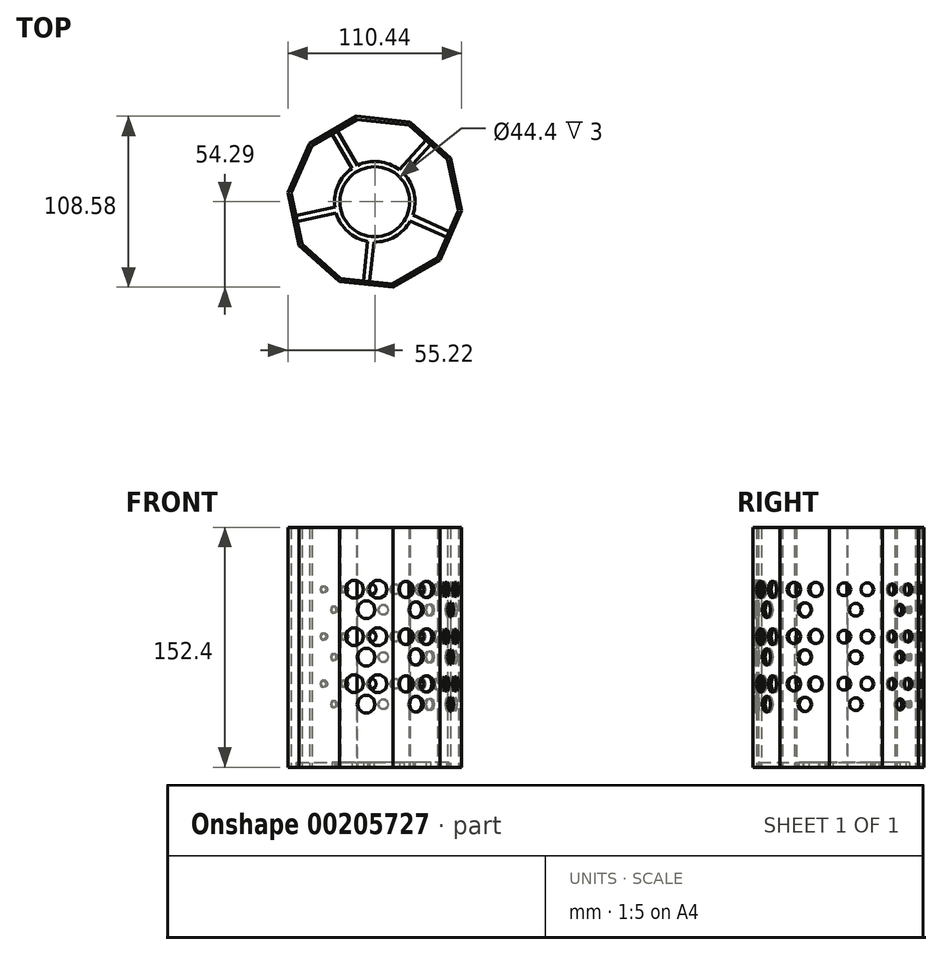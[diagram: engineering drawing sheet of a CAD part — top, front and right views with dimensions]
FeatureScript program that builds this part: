
annotation { "Feature Type Name" : "Feature", "Feature Type Description" : "" }
export const myFeature = defineFeature(function(context is Context, id is Id, definition is map)
    precondition{}
    {
        {
            var Q0;
            Q0=qCreatedBy(makeId("Top.planeOp"),FACE);
            var sketch = newSketch(context, id + "F0", { "sketchPlane" : qUnion([Q0])});
            skCircle(sketch, "E0.cCircle", {"center": v(0, 0) * mm, "radius": 50.8 * mm, "construction": true});
            skLineSegment(sketch, "E0.0", {"start": v(-39.74, 35.7) * mm, "end": v(-11.17, 52.23) * mm});
            skLineSegment(sketch, "E0.1", {"start": v(-11.17, 52.23) * mm, "end": v(21.67, 48.82) * mm});
            skLineSegment(sketch, "E0.2", {"start": v(21.67, 48.82) * mm, "end": v(46.23, 26.76) * mm});
            skLineSegment(sketch, "E0.3", {"start": v(46.23, 26.76) * mm, "end": v(53.13, -5.52) * mm});
            skLineSegment(sketch, "E0.4", {"start": v(53.13, -5.52) * mm, "end": v(39.74, -35.7) * mm});
            skLineSegment(sketch, "E0.5", {"start": v(39.74, -35.7) * mm, "end": v(11.17, -52.23) * mm});
            skLineSegment(sketch, "E0.6", {"start": v(11.17, -52.23) * mm, "end": v(-21.67, -48.82) * mm});
            skLineSegment(sketch, "E0.7", {"start": v(-21.67, -48.82) * mm, "end": v(-46.23, -26.76) * mm});
            skLineSegment(sketch, "E0.8", {"start": v(-46.23, -26.76) * mm, "end": v(-53.13, 5.52) * mm});
            skLineSegment(sketch, "E0.9", {"start": v(-53.13, 5.52) * mm, "end": v(-39.74, 35.7) * mm});
            skPoint(sketch, "E0.0.midPoint", {"position": v(-25.45, 43.96) * mm});
            skLineSegment(sketch, "E1.0", {"start": v(-41.3, 37.1) * mm, "end": v(-11.6, 54.3) * mm});
            skLineSegment(sketch, "E1.1", {"start": v(-55.22, 5.74) * mm, "end": v(-41.3, 37.1) * mm});
            skLineSegment(sketch, "E1.2", {"start": v(-11.6, 54.3) * mm, "end": v(22.52, 50.74) * mm});
            skLineSegment(sketch, "E1.3", {"start": v(-48.05, -27.82) * mm, "end": v(-55.22, 5.74) * mm});
            skLineSegment(sketch, "E1.4", {"start": v(-22.52, -50.74) * mm, "end": v(-48.05, -27.82) * mm});
            skLineSegment(sketch, "E1.5", {"start": v(11.6, -54.3) * mm, "end": v(-22.52, -50.74) * mm});
            skLineSegment(sketch, "E1.6", {"start": v(22.52, 50.74) * mm, "end": v(48.05, 27.82) * mm});
            skLineSegment(sketch, "E1.7", {"start": v(48.05, 27.82) * mm, "end": v(55.22, -5.74) * mm});
            skLineSegment(sketch, "E1.8", {"start": v(55.22, -5.74) * mm, "end": v(41.3, -37.1) * mm});
            skLineSegment(sketch, "E1.9", {"start": v(41.3, -37.1) * mm, "end": v(11.6, -54.3) * mm});
            skSolve(sketch);
        }
        {
            var Q0;
            Q0=makeQuery(id+"F0.imprint","IMPRINT",FACE,{"disambiguationData":[TD([[makeQuery(id+"F0.imprint","IMPRINT",EDGE,{"derivedFrom":sQuery(id+"F0.wireOp",EDGE,"E0.0")}),1.0]])]});
            extrude(context, id + "F1", {"entities" : qUnion([Q0]), "depth" : 152.4 * mm});
        }
        {
            var Q0;
            Q0=makeQuery(id+"F1.opExtrude","SWEPT_FACE",FACE,{"disambiguationData":[OSD([sQuery(id+"F0.wireOp",EDGE,"E1.5")])]});
            var sketch = newSketch(context, id + "F2", { "sketchPlane" : qUnion([Q0])});
            skCircle(sketch, "E2.cCircle", {"center": v(0, 40) * mm, "radius": 5.5 * mm, "construction": true});
            skLineSegment(sketch, "E2.0", {"start": v(-1.79, 45.5) * mm, "end": v(1.79, 45.5) * mm});
            skLineSegment(sketch, "E2.1", {"start": v(1.79, 45.5) * mm, "end": v(4.68, 43.4) * mm});
            skLineSegment(sketch, "E2.2", {"start": v(4.68, 43.4) * mm, "end": v(5.78, 40) * mm});
            skLineSegment(sketch, "E2.3", {"start": v(5.78, 40) * mm, "end": v(4.68, 36.6) * mm});
            skLineSegment(sketch, "E2.4", {"start": v(4.68, 36.6) * mm, "end": v(1.79, 34.5) * mm});
            skLineSegment(sketch, "E2.5", {"start": v(1.79, 34.5) * mm, "end": v(-1.79, 34.5) * mm});
            skLineSegment(sketch, "E2.6", {"start": v(-1.79, 34.5) * mm, "end": v(-4.68, 36.6) * mm});
            skLineSegment(sketch, "E2.7", {"start": v(-4.68, 36.6) * mm, "end": v(-5.78, 40) * mm});
            skLineSegment(sketch, "E2.8", {"start": v(-5.78, 40) * mm, "end": v(-4.68, 43.4) * mm});
            skLineSegment(sketch, "E2.9", {"start": v(-4.68, 43.4) * mm, "end": v(-1.79, 45.5) * mm});
            skPoint(sketch, "E2.0.midPoint", {"position": v(0, 45.5) * mm});
            skCircle(sketch, "E3.cCircle", {"center": v(-7.5, 53) * mm, "radius": 5.5 * mm, "construction": true});
            skLineSegment(sketch, "E3.0", {"start": v(-9.29, 58.5) * mm, "end": v(-5.71, 58.5) * mm});
            skLineSegment(sketch, "E3.1", {"start": v(-5.71, 58.5) * mm, "end": v(-2.82, 56.39) * mm});
            skLineSegment(sketch, "E3.2", {"start": v(-2.82, 56.39) * mm, "end": v(-1.72, 53) * mm});
            skLineSegment(sketch, "E3.3", {"start": v(-1.72, 53) * mm, "end": v(-2.82, 49.6) * mm});
            skLineSegment(sketch, "E3.4", {"start": v(-2.82, 49.6) * mm, "end": v(-5.71, 47.5) * mm});
            skLineSegment(sketch, "E3.5", {"start": v(-5.71, 47.5) * mm, "end": v(-9.29, 47.5) * mm});
            skLineSegment(sketch, "E3.6", {"start": v(-9.29, 47.5) * mm, "end": v(-12.18, 49.6) * mm});
            skLineSegment(sketch, "E3.7", {"start": v(-12.18, 49.6) * mm, "end": v(-13.28, 53) * mm});
            skLineSegment(sketch, "E3.8", {"start": v(-13.28, 53) * mm, "end": v(-12.18, 56.39) * mm});
            skLineSegment(sketch, "E3.9", {"start": v(-12.18, 56.39) * mm, "end": v(-9.29, 58.5) * mm});
            skPoint(sketch, "E3.0.midPoint", {"position": v(-7.5, 58.5) * mm});
            skCircle(sketch, "E4.cCircle", {"center": v(7.5, 53) * mm, "radius": 5.5 * mm, "construction": true});
            skLineSegment(sketch, "E4.0", {"start": v(5.71, 58.5) * mm, "end": v(9.29, 58.5) * mm});
            skLineSegment(sketch, "E4.1", {"start": v(9.29, 58.5) * mm, "end": v(12.18, 56.39) * mm});
            skLineSegment(sketch, "E4.2", {"start": v(12.18, 56.39) * mm, "end": v(13.28, 53) * mm});
            skLineSegment(sketch, "E4.3", {"start": v(13.28, 53) * mm, "end": v(12.18, 49.6) * mm});
            skLineSegment(sketch, "E4.4", {"start": v(12.18, 49.6) * mm, "end": v(9.29, 47.5) * mm});
            skLineSegment(sketch, "E4.5", {"start": v(9.29, 47.5) * mm, "end": v(5.71, 47.5) * mm});
            skLineSegment(sketch, "E4.6", {"start": v(5.71, 47.5) * mm, "end": v(2.82, 49.6) * mm});
            skLineSegment(sketch, "E4.7", {"start": v(2.82, 49.6) * mm, "end": v(1.72, 53) * mm});
            skLineSegment(sketch, "E4.8", {"start": v(1.72, 53) * mm, "end": v(2.82, 56.39) * mm});
            skLineSegment(sketch, "E4.9", {"start": v(2.82, 56.39) * mm, "end": v(5.71, 58.5) * mm});
            skPoint(sketch, "E4.0.midPoint", {"position": v(7.5, 58.5) * mm});
            skLineSegment(sketch, "E5", {"start": v(7.5, 53) * mm, "end": v(-7.5, 53) * mm, "construction": true});
            skLineSegment(sketch, "E6", {"start": v(0, 40) * mm, "end": v(-7.5, 53) * mm, "construction": true});
            skLineSegment(sketch, "E7", {"start": v(0, 40) * mm, "end": v(7.5, 53) * mm, "construction": true});
            skLineSegment(sketch, "E8", {"start": v(0, 0) * mm, "end": v(0, 152.4) * mm, "construction": true});
            skPoint(sketch, "E9.0.1.0", {"position": v(0, 75.5) * mm});
            skLineSegment(sketch, "E9.0.1.1", {"start": v(0, 70) * mm, "end": v(7.5, 83) * mm, "construction": true});
            skLineSegment(sketch, "E9.0.1.2", {"start": v(0, 70) * mm, "end": v(-7.5, 83) * mm, "construction": true});
            skLineSegment(sketch, "E9.0.1.3", {"start": v(7.5, 83) * mm, "end": v(-7.5, 83) * mm, "construction": true});
            skPoint(sketch, "E9.0.1.4", {"position": v(7.5, 88.5) * mm});
            skPoint(sketch, "E9.0.1.5", {"position": v(-7.5, 88.5) * mm});
            skLineSegment(sketch, "E9.0.1.6", {"start": v(-2.82, 86.39) * mm, "end": v(-1.72, 83) * mm});
            skLineSegment(sketch, "E9.0.1.7", {"start": v(13.28, 83) * mm, "end": v(12.18, 79.6) * mm});
            skLineSegment(sketch, "E9.0.1.8", {"start": v(2.82, 86.39) * mm, "end": v(5.71, 88.5) * mm});
            skCircle(sketch, "E9.0.1.9", {"center": v(7.5, 83) * mm, "radius": 5.5 * mm, "construction": true});
            skLineSegment(sketch, "E9.0.1.10", {"start": v(2.82, 79.6) * mm, "end": v(1.72, 83) * mm});
            skLineSegment(sketch, "E9.0.1.11", {"start": v(-5.78, 70) * mm, "end": v(-4.68, 73.4) * mm});
            skLineSegment(sketch, "E9.0.1.12", {"start": v(4.68, 73.4) * mm, "end": v(5.78, 70) * mm});
            skLineSegment(sketch, "E9.0.1.13", {"start": v(-9.29, 77.5) * mm, "end": v(-12.18, 79.6) * mm});
            skLineSegment(sketch, "E9.0.1.14", {"start": v(1.79, 75.5) * mm, "end": v(4.68, 73.4) * mm});
            skLineSegment(sketch, "E9.0.1.15", {"start": v(-2.82, 79.6) * mm, "end": v(-5.71, 77.5) * mm});
            skLineSegment(sketch, "E9.0.1.16", {"start": v(-9.29, 88.5) * mm, "end": v(-5.71, 88.5) * mm});
            skLineSegment(sketch, "E9.0.1.17", {"start": v(-5.71, 88.5) * mm, "end": v(-2.82, 86.39) * mm});
            skCircle(sketch, "E9.0.1.18", {"center": v(-7.5, 83) * mm, "radius": 5.5 * mm, "construction": true});
            skLineSegment(sketch, "E9.0.1.19", {"start": v(12.18, 79.6) * mm, "end": v(9.29, 77.5) * mm});
            skLineSegment(sketch, "E9.0.1.20", {"start": v(-12.18, 86.39) * mm, "end": v(-9.29, 88.5) * mm});
            skLineSegment(sketch, "E9.0.1.21", {"start": v(12.18, 86.39) * mm, "end": v(13.28, 83) * mm});
            skLineSegment(sketch, "E9.0.1.22", {"start": v(-4.68, 66.6) * mm, "end": v(-5.78, 70) * mm});
            skLineSegment(sketch, "E9.0.1.23", {"start": v(-13.28, 83) * mm, "end": v(-12.18, 86.39) * mm});
            skLineSegment(sketch, "E9.0.1.24", {"start": v(9.29, 77.5) * mm, "end": v(5.71, 77.5) * mm});
            skLineSegment(sketch, "E9.0.1.25", {"start": v(-4.68, 73.4) * mm, "end": v(-1.79, 75.5) * mm});
            skLineSegment(sketch, "E9.0.1.26", {"start": v(-12.18, 79.6) * mm, "end": v(-13.28, 83) * mm});
            skLineSegment(sketch, "E9.0.1.27", {"start": v(-1.79, 64.5) * mm, "end": v(-4.68, 66.6) * mm});
            skLineSegment(sketch, "E9.0.1.28", {"start": v(5.71, 77.5) * mm, "end": v(2.82, 79.6) * mm});
            skCircle(sketch, "E9.0.1.29", {"center": v(0, 70) * mm, "radius": 5.5 * mm, "construction": true});
            skLineSegment(sketch, "E9.0.1.30", {"start": v(-1.72, 83) * mm, "end": v(-2.82, 79.6) * mm});
            skLineSegment(sketch, "E9.0.1.31", {"start": v(1.72, 83) * mm, "end": v(2.82, 86.39) * mm});
            skLineSegment(sketch, "E9.0.1.32", {"start": v(9.29, 88.5) * mm, "end": v(12.18, 86.39) * mm});
            skLineSegment(sketch, "E9.0.1.33", {"start": v(5.78, 70) * mm, "end": v(4.68, 66.6) * mm});
            skLineSegment(sketch, "E9.0.1.34", {"start": v(4.68, 66.6) * mm, "end": v(1.79, 64.5) * mm});
            skLineSegment(sketch, "E9.0.1.35", {"start": v(5.71, 88.5) * mm, "end": v(9.29, 88.5) * mm});
            skLineSegment(sketch, "E9.0.1.36", {"start": v(-5.71, 77.5) * mm, "end": v(-9.29, 77.5) * mm});
            skLineSegment(sketch, "E9.0.1.37", {"start": v(1.79, 64.5) * mm, "end": v(-1.79, 64.5) * mm});
            skLineSegment(sketch, "E9.0.1.38", {"start": v(-1.79, 75.5) * mm, "end": v(1.79, 75.5) * mm});
            skPoint(sketch, "E9.0.2.0", {"position": v(0, 105.5) * mm});
            skLineSegment(sketch, "E9.0.2.1", {"start": v(0, 100) * mm, "end": v(7.5, 113) * mm, "construction": true});
            skLineSegment(sketch, "E9.0.2.2", {"start": v(0, 100) * mm, "end": v(-7.5, 113) * mm, "construction": true});
            skLineSegment(sketch, "E9.0.2.3", {"start": v(7.5, 113) * mm, "end": v(-7.5, 113) * mm, "construction": true});
            skPoint(sketch, "E9.0.2.4", {"position": v(7.5, 118.5) * mm});
            skPoint(sketch, "E9.0.2.5", {"position": v(-7.5, 118.5) * mm});
            skLineSegment(sketch, "E9.0.2.6", {"start": v(-2.82, 116.39) * mm, "end": v(-1.72, 113) * mm});
            skLineSegment(sketch, "E9.0.2.7", {"start": v(13.28, 113) * mm, "end": v(12.18, 109.6) * mm});
            skLineSegment(sketch, "E9.0.2.8", {"start": v(2.82, 116.39) * mm, "end": v(5.71, 118.5) * mm});
            skCircle(sketch, "E9.0.2.9", {"center": v(7.5, 113) * mm, "radius": 5.5 * mm, "construction": true});
            skLineSegment(sketch, "E9.0.2.10", {"start": v(2.82, 109.6) * mm, "end": v(1.72, 113) * mm});
            skLineSegment(sketch, "E9.0.2.11", {"start": v(-5.78, 100) * mm, "end": v(-4.68, 103.4) * mm});
            skLineSegment(sketch, "E9.0.2.12", {"start": v(4.68, 103.4) * mm, "end": v(5.78, 100) * mm});
            skLineSegment(sketch, "E9.0.2.13", {"start": v(-9.29, 107.5) * mm, "end": v(-12.18, 109.6) * mm});
            skLineSegment(sketch, "E9.0.2.14", {"start": v(1.79, 105.5) * mm, "end": v(4.68, 103.4) * mm});
            skLineSegment(sketch, "E9.0.2.15", {"start": v(-2.82, 109.6) * mm, "end": v(-5.71, 107.5) * mm});
            skLineSegment(sketch, "E9.0.2.16", {"start": v(-9.29, 118.5) * mm, "end": v(-5.71, 118.5) * mm});
            skLineSegment(sketch, "E9.0.2.17", {"start": v(-5.71, 118.5) * mm, "end": v(-2.82, 116.39) * mm});
            skCircle(sketch, "E9.0.2.18", {"center": v(-7.5, 113) * mm, "radius": 5.5 * mm, "construction": true});
            skLineSegment(sketch, "E9.0.2.19", {"start": v(12.18, 109.6) * mm, "end": v(9.29, 107.5) * mm});
            skLineSegment(sketch, "E9.0.2.20", {"start": v(-12.18, 116.39) * mm, "end": v(-9.29, 118.5) * mm});
            skLineSegment(sketch, "E9.0.2.21", {"start": v(12.18, 116.39) * mm, "end": v(13.28, 113) * mm});
            skLineSegment(sketch, "E9.0.2.22", {"start": v(-4.68, 96.6) * mm, "end": v(-5.78, 100) * mm});
            skLineSegment(sketch, "E9.0.2.23", {"start": v(-13.28, 113) * mm, "end": v(-12.18, 116.39) * mm});
            skLineSegment(sketch, "E9.0.2.24", {"start": v(9.29, 107.5) * mm, "end": v(5.71, 107.5) * mm});
            skLineSegment(sketch, "E9.0.2.25", {"start": v(-4.68, 103.4) * mm, "end": v(-1.79, 105.5) * mm});
            skLineSegment(sketch, "E9.0.2.26", {"start": v(-12.18, 109.6) * mm, "end": v(-13.28, 113) * mm});
            skLineSegment(sketch, "E9.0.2.27", {"start": v(-1.79, 94.5) * mm, "end": v(-4.68, 96.6) * mm});
            skLineSegment(sketch, "E9.0.2.28", {"start": v(5.71, 107.5) * mm, "end": v(2.82, 109.6) * mm});
            skCircle(sketch, "E9.0.2.29", {"center": v(0, 100) * mm, "radius": 5.5 * mm, "construction": true});
            skLineSegment(sketch, "E9.0.2.30", {"start": v(-1.72, 113) * mm, "end": v(-2.82, 109.6) * mm});
            skLineSegment(sketch, "E9.0.2.31", {"start": v(1.72, 113) * mm, "end": v(2.82, 116.39) * mm});
            skLineSegment(sketch, "E9.0.2.32", {"start": v(9.29, 118.5) * mm, "end": v(12.18, 116.39) * mm});
            skLineSegment(sketch, "E9.0.2.33", {"start": v(5.78, 100) * mm, "end": v(4.68, 96.6) * mm});
            skLineSegment(sketch, "E9.0.2.34", {"start": v(4.68, 96.6) * mm, "end": v(1.79, 94.5) * mm});
            skLineSegment(sketch, "E9.0.2.35", {"start": v(5.71, 118.5) * mm, "end": v(9.29, 118.5) * mm});
            skLineSegment(sketch, "E9.0.2.36", {"start": v(-5.71, 107.5) * mm, "end": v(-9.29, 107.5) * mm});
            skLineSegment(sketch, "E9.0.2.37", {"start": v(1.79, 94.5) * mm, "end": v(-1.79, 94.5) * mm});
            skLineSegment(sketch, "E9.0.2.38", {"start": v(-1.79, 105.5) * mm, "end": v(1.79, 105.5) * mm});
            skLineSegment(sketch, "E9.direction1", {"start": v(-4.68, 36.6) * mm, "end": v(20.32, 36.6) * mm, "construction": true});
            skLineSegment(sketch, "E9.direction2", {"start": v(-4.68, 36.6) * mm, "end": v(-4.68, 66.6) * mm, "construction": true});
            skSolve(sketch);
        }
        {
            var Q0;
            Q0=makeQuery(id+"F1.opExtrude","SWEPT_FACE",FACE,{"disambiguationData":[OSD([sQuery(id+"F0.wireOp",EDGE,"E1.9")])]});
            var sketch = newSketch(context, id + "F3", { "sketchPlane" : qUnion([Q0])});
            skCircle(sketch, "E10.cCircle", {"center": v(0, 40) * mm, "radius": 5 * mm, "construction": true});
            skLineSegment(sketch, "E10.0", {"start": v(-1.62, 45) * mm, "end": v(1.62, 45) * mm});
            skLineSegment(sketch, "E10.1", {"start": v(1.62, 45) * mm, "end": v(4.25, 43.1) * mm});
            skLineSegment(sketch, "E10.2", {"start": v(4.25, 43.1) * mm, "end": v(5.26, 40) * mm});
            skLineSegment(sketch, "E10.3", {"start": v(5.26, 40) * mm, "end": v(4.25, 36.9) * mm});
            skLineSegment(sketch, "E10.4", {"start": v(4.25, 36.9) * mm, "end": v(1.62, 35) * mm});
            skLineSegment(sketch, "E10.5", {"start": v(1.62, 35) * mm, "end": v(-1.62, 35) * mm});
            skLineSegment(sketch, "E10.6", {"start": v(-1.62, 35) * mm, "end": v(-4.25, 36.9) * mm});
            skLineSegment(sketch, "E10.7", {"start": v(-4.25, 36.9) * mm, "end": v(-5.26, 40) * mm});
            skLineSegment(sketch, "E10.8", {"start": v(-5.26, 40) * mm, "end": v(-4.25, 43.1) * mm});
            skLineSegment(sketch, "E10.9", {"start": v(-4.25, 43.1) * mm, "end": v(-1.62, 45) * mm});
            skPoint(sketch, "E10.0.midPoint", {"position": v(0, 45) * mm});
            skCircle(sketch, "E11.cCircle", {"center": v(-7.5, 53) * mm, "radius": 5 * mm, "construction": true});
            skLineSegment(sketch, "E11.0", {"start": v(-9.12, 58) * mm, "end": v(-5.88, 58) * mm});
            skLineSegment(sketch, "E11.1", {"start": v(-5.88, 58) * mm, "end": v(-3.25, 56.08) * mm});
            skLineSegment(sketch, "E11.2", {"start": v(-3.25, 56.08) * mm, "end": v(-2.24, 53) * mm});
            skLineSegment(sketch, "E11.3", {"start": v(-2.24, 53) * mm, "end": v(-3.25, 49.9) * mm});
            skLineSegment(sketch, "E11.4", {"start": v(-3.25, 49.9) * mm, "end": v(-5.88, 48) * mm});
            skLineSegment(sketch, "E11.5", {"start": v(-5.88, 48) * mm, "end": v(-9.12, 48) * mm});
            skLineSegment(sketch, "E11.6", {"start": v(-9.12, 48) * mm, "end": v(-11.75, 49.9) * mm});
            skLineSegment(sketch, "E11.7", {"start": v(-11.75, 49.9) * mm, "end": v(-12.76, 53) * mm});
            skLineSegment(sketch, "E11.8", {"start": v(-12.76, 53) * mm, "end": v(-11.75, 56.08) * mm});
            skLineSegment(sketch, "E11.9", {"start": v(-11.75, 56.08) * mm, "end": v(-9.12, 58) * mm});
            skPoint(sketch, "E11.0.midPoint", {"position": v(-7.5, 58) * mm});
            skCircle(sketch, "E12.cCircle", {"center": v(7.5, 53) * mm, "radius": 5 * mm, "construction": true});
            skLineSegment(sketch, "E12.0", {"start": v(5.88, 58) * mm, "end": v(9.12, 58) * mm});
            skLineSegment(sketch, "E12.1", {"start": v(9.12, 58) * mm, "end": v(11.75, 56.08) * mm});
            skLineSegment(sketch, "E12.2", {"start": v(11.75, 56.08) * mm, "end": v(12.76, 53) * mm});
            skLineSegment(sketch, "E12.3", {"start": v(12.76, 53) * mm, "end": v(11.75, 49.9) * mm});
            skLineSegment(sketch, "E12.4", {"start": v(11.75, 49.9) * mm, "end": v(9.12, 48) * mm});
            skLineSegment(sketch, "E12.5", {"start": v(9.12, 48) * mm, "end": v(5.88, 48) * mm});
            skLineSegment(sketch, "E12.6", {"start": v(5.88, 48) * mm, "end": v(3.25, 49.9) * mm});
            skLineSegment(sketch, "E12.7", {"start": v(3.25, 49.9) * mm, "end": v(2.24, 53) * mm});
            skLineSegment(sketch, "E12.8", {"start": v(2.24, 53) * mm, "end": v(3.25, 56.08) * mm});
            skLineSegment(sketch, "E12.9", {"start": v(3.25, 56.08) * mm, "end": v(5.88, 58) * mm});
            skPoint(sketch, "E12.0.midPoint", {"position": v(7.5, 58) * mm});
            skLineSegment(sketch, "E13", {"start": v(7.5, 53) * mm, "end": v(-7.5, 53) * mm, "construction": true});
            skLineSegment(sketch, "E14", {"start": v(0, 40) * mm, "end": v(-7.5, 53) * mm, "construction": true});
            skLineSegment(sketch, "E15", {"start": v(0, 40) * mm, "end": v(7.5, 53) * mm, "construction": true});
            skLineSegment(sketch, "E16", {"start": v(0, 0) * mm, "end": v(0, 152.4) * mm, "construction": true});
            skLineSegment(sketch, "E17.direction1", {"start": v(-4.25, 36.9) * mm, "end": v(20.75, 36.9) * mm, "construction": true});
            skLineSegment(sketch, "E17.direction2", {"start": v(-4.25, 36.9) * mm, "end": v(-4.25, 66.9) * mm, "construction": true});
            skPoint(sketch, "E18.0.0.1", {"position": v(0, 75) * mm});
            skLineSegment(sketch, "E18.1.0.1", {"start": v(0, 70) * mm, "end": v(7.5, 83) * mm, "construction": true});
            skLineSegment(sketch, "E18.4.0.1", {"start": v(0, 70) * mm, "end": v(-7.5, 83) * mm, "construction": true});
            skLineSegment(sketch, "E18.7.0.1", {"start": v(7.5, 83) * mm, "end": v(-7.5, 83) * mm, "construction": true});
            skPoint(sketch, "E18.10.0.1", {"position": v(7.5, 88) * mm});
            skPoint(sketch, "E18.11.0.1", {"position": v(-7.5, 88) * mm});
            skLineSegment(sketch, "E18.12.0.1", {"start": v(-3.25, 86.08) * mm, "end": v(-2.24, 83) * mm});
            skLineSegment(sketch, "E18.15.0.1", {"start": v(12.76, 83) * mm, "end": v(11.75, 79.9) * mm});
            skLineSegment(sketch, "E18.18.0.1", {"start": v(3.25, 86.08) * mm, "end": v(5.88, 88) * mm});
            skCircle(sketch, "E18.21.0.1", {"center": v(7.5, 83) * mm, "radius": 5 * mm, "construction": true});
            skLineSegment(sketch, "E18.23.0.1", {"start": v(3.25, 79.9) * mm, "end": v(2.24, 83) * mm});
            skLineSegment(sketch, "E18.26.0.1", {"start": v(-5.26, 70) * mm, "end": v(-4.25, 73.1) * mm});
            skLineSegment(sketch, "E18.29.0.1", {"start": v(4.25, 73.1) * mm, "end": v(5.26, 70) * mm});
            skLineSegment(sketch, "E18.32.0.1", {"start": v(-9.12, 78) * mm, "end": v(-11.75, 79.9) * mm});
            skLineSegment(sketch, "E18.35.0.1", {"start": v(1.62, 75) * mm, "end": v(4.25, 73.1) * mm});
            skLineSegment(sketch, "E18.38.0.1", {"start": v(-3.25, 79.9) * mm, "end": v(-5.88, 78) * mm});
            skLineSegment(sketch, "E18.41.0.1", {"start": v(-9.12, 88) * mm, "end": v(-5.88, 88) * mm});
            skLineSegment(sketch, "E18.44.0.1", {"start": v(-5.88, 88) * mm, "end": v(-3.25, 86.08) * mm});
            skCircle(sketch, "E18.47.0.1", {"center": v(-7.5, 83) * mm, "radius": 5 * mm, "construction": true});
            skLineSegment(sketch, "E18.49.0.1", {"start": v(11.75, 79.9) * mm, "end": v(9.12, 78) * mm});
            skLineSegment(sketch, "E18.52.0.1", {"start": v(-11.75, 86.08) * mm, "end": v(-9.12, 88) * mm});
            skLineSegment(sketch, "E18.55.0.1", {"start": v(11.75, 86.08) * mm, "end": v(12.76, 83) * mm});
            skLineSegment(sketch, "E18.58.0.1", {"start": v(-4.25, 66.9) * mm, "end": v(-5.26, 70) * mm});
            skLineSegment(sketch, "E18.61.0.1", {"start": v(-12.76, 83) * mm, "end": v(-11.75, 86.08) * mm});
            skLineSegment(sketch, "E18.64.0.1", {"start": v(9.12, 78) * mm, "end": v(5.88, 78) * mm});
            skLineSegment(sketch, "E18.67.0.1", {"start": v(-4.25, 73.1) * mm, "end": v(-1.62, 75) * mm});
            skLineSegment(sketch, "E18.70.0.1", {"start": v(-11.75, 79.9) * mm, "end": v(-12.76, 83) * mm});
            skLineSegment(sketch, "E18.73.0.1", {"start": v(-1.62, 65) * mm, "end": v(-4.25, 66.9) * mm});
            skLineSegment(sketch, "E18.76.0.1", {"start": v(5.88, 78) * mm, "end": v(3.25, 79.9) * mm});
            skCircle(sketch, "E18.79.0.1", {"center": v(0, 70) * mm, "radius": 5 * mm, "construction": true});
            skLineSegment(sketch, "E18.81.0.1", {"start": v(-2.24, 83) * mm, "end": v(-3.25, 79.9) * mm});
            skLineSegment(sketch, "E18.84.0.1", {"start": v(2.24, 83) * mm, "end": v(3.25, 86.08) * mm});
            skLineSegment(sketch, "E18.87.0.1", {"start": v(9.12, 88) * mm, "end": v(11.75, 86.08) * mm});
            skLineSegment(sketch, "E18.90.0.1", {"start": v(5.26, 70) * mm, "end": v(4.25, 66.9) * mm});
            skLineSegment(sketch, "E18.93.0.1", {"start": v(4.25, 66.9) * mm, "end": v(1.62, 65) * mm});
            skLineSegment(sketch, "E18.96.0.1", {"start": v(5.88, 88) * mm, "end": v(9.12, 88) * mm});
            skLineSegment(sketch, "E18.99.0.1", {"start": v(-5.88, 78) * mm, "end": v(-9.12, 78) * mm});
            skLineSegment(sketch, "E18.102.0.1", {"start": v(1.62, 65) * mm, "end": v(-1.62, 65) * mm});
            skLineSegment(sketch, "E18.105.0.1", {"start": v(-1.62, 75) * mm, "end": v(1.62, 75) * mm});
            skPoint(sketch, "E18.0.0.2", {"position": v(0, 105) * mm});
            skLineSegment(sketch, "E18.1.0.2", {"start": v(0, 100) * mm, "end": v(7.5, 113) * mm, "construction": true});
            skLineSegment(sketch, "E18.4.0.2", {"start": v(0, 100) * mm, "end": v(-7.5, 113) * mm, "construction": true});
            skLineSegment(sketch, "E18.7.0.2", {"start": v(7.5, 113) * mm, "end": v(-7.5, 113) * mm, "construction": true});
            skPoint(sketch, "E18.10.0.2", {"position": v(7.5, 118) * mm});
            skPoint(sketch, "E18.11.0.2", {"position": v(-7.5, 118) * mm});
            skLineSegment(sketch, "E18.12.0.2", {"start": v(-3.25, 116.08) * mm, "end": v(-2.24, 113) * mm});
            skLineSegment(sketch, "E18.15.0.2", {"start": v(12.76, 113) * mm, "end": v(11.75, 109.9) * mm});
            skLineSegment(sketch, "E18.18.0.2", {"start": v(3.25, 116.08) * mm, "end": v(5.88, 118) * mm});
            skCircle(sketch, "E18.21.0.2", {"center": v(7.5, 113) * mm, "radius": 5 * mm, "construction": true});
            skLineSegment(sketch, "E18.23.0.2", {"start": v(3.25, 109.9) * mm, "end": v(2.24, 113) * mm});
            skLineSegment(sketch, "E18.26.0.2", {"start": v(-5.26, 100) * mm, "end": v(-4.25, 103.1) * mm});
            skLineSegment(sketch, "E18.29.0.2", {"start": v(4.25, 103.1) * mm, "end": v(5.26, 100) * mm});
            skLineSegment(sketch, "E18.32.0.2", {"start": v(-9.12, 108) * mm, "end": v(-11.75, 109.9) * mm});
            skLineSegment(sketch, "E18.35.0.2", {"start": v(1.62, 105) * mm, "end": v(4.25, 103.1) * mm});
            skLineSegment(sketch, "E18.38.0.2", {"start": v(-3.25, 109.9) * mm, "end": v(-5.88, 108) * mm});
            skLineSegment(sketch, "E18.41.0.2", {"start": v(-9.12, 118) * mm, "end": v(-5.88, 118) * mm});
            skLineSegment(sketch, "E18.44.0.2", {"start": v(-5.88, 118) * mm, "end": v(-3.25, 116.08) * mm});
            skCircle(sketch, "E18.47.0.2", {"center": v(-7.5, 113) * mm, "radius": 5 * mm, "construction": true});
            skLineSegment(sketch, "E18.49.0.2", {"start": v(11.75, 109.9) * mm, "end": v(9.12, 108) * mm});
            skLineSegment(sketch, "E18.52.0.2", {"start": v(-11.75, 116.08) * mm, "end": v(-9.12, 118) * mm});
            skLineSegment(sketch, "E18.55.0.2", {"start": v(11.75, 116.08) * mm, "end": v(12.76, 113) * mm});
            skLineSegment(sketch, "E18.58.0.2", {"start": v(-4.25, 96.9) * mm, "end": v(-5.26, 100) * mm});
            skLineSegment(sketch, "E18.61.0.2", {"start": v(-12.76, 113) * mm, "end": v(-11.75, 116.08) * mm});
            skLineSegment(sketch, "E18.64.0.2", {"start": v(9.12, 108) * mm, "end": v(5.88, 108) * mm});
            skLineSegment(sketch, "E18.67.0.2", {"start": v(-4.25, 103.1) * mm, "end": v(-1.62, 105) * mm});
            skLineSegment(sketch, "E18.70.0.2", {"start": v(-11.75, 109.9) * mm, "end": v(-12.76, 113) * mm});
            skLineSegment(sketch, "E18.73.0.2", {"start": v(-1.62, 95) * mm, "end": v(-4.25, 96.9) * mm});
            skLineSegment(sketch, "E18.76.0.2", {"start": v(5.88, 108) * mm, "end": v(3.25, 109.9) * mm});
            skCircle(sketch, "E18.79.0.2", {"center": v(0, 100) * mm, "radius": 5 * mm, "construction": true});
            skLineSegment(sketch, "E18.81.0.2", {"start": v(-2.24, 113) * mm, "end": v(-3.25, 109.9) * mm});
            skLineSegment(sketch, "E18.84.0.2", {"start": v(2.24, 113) * mm, "end": v(3.25, 116.08) * mm});
            skLineSegment(sketch, "E18.87.0.2", {"start": v(9.12, 118) * mm, "end": v(11.75, 116.08) * mm});
            skLineSegment(sketch, "E18.90.0.2", {"start": v(5.26, 100) * mm, "end": v(4.25, 96.9) * mm});
            skLineSegment(sketch, "E18.93.0.2", {"start": v(4.25, 96.9) * mm, "end": v(1.62, 95) * mm});
            skLineSegment(sketch, "E18.96.0.2", {"start": v(5.88, 118) * mm, "end": v(9.12, 118) * mm});
            skLineSegment(sketch, "E18.99.0.2", {"start": v(-5.88, 108) * mm, "end": v(-9.12, 108) * mm});
            skLineSegment(sketch, "E18.102.0.2", {"start": v(1.62, 95) * mm, "end": v(-1.62, 95) * mm});
            skLineSegment(sketch, "E18.105.0.2", {"start": v(-1.62, 105) * mm, "end": v(1.62, 105) * mm});
            skSolve(sketch);
        }
        {
            var Q0;
            Q0=makeQuery(id+"F1.opExtrude","SWEPT_FACE",FACE,{"disambiguationData":[OSD([sQuery(id+"F0.wireOp",EDGE,"E1.8")])]});
            var sketch = newSketch(context, id + "F4", { "sketchPlane" : qUnion([Q0])});
            skCircle(sketch, "E19.cCircle", {"center": v(-0.1, 40) * mm, "radius": 4.5 * mm, "construction": true});
            skLineSegment(sketch, "E19.0", {"start": v(-1.56, 44.5) * mm, "end": v(1.37, 44.5) * mm});
            skLineSegment(sketch, "E19.1", {"start": v(1.37, 44.5) * mm, "end": v(3.73, 42.78) * mm});
            skLineSegment(sketch, "E19.2", {"start": v(3.73, 42.78) * mm, "end": v(4.64, 40) * mm});
            skLineSegment(sketch, "E19.3", {"start": v(4.64, 40) * mm, "end": v(3.73, 37.22) * mm});
            skLineSegment(sketch, "E19.4", {"start": v(3.73, 37.22) * mm, "end": v(1.37, 35.5) * mm});
            skLineSegment(sketch, "E19.5", {"start": v(1.37, 35.5) * mm, "end": v(-1.56, 35.5) * mm});
            skLineSegment(sketch, "E19.6", {"start": v(-1.56, 35.5) * mm, "end": v(-3.92, 37.22) * mm});
            skLineSegment(sketch, "E19.7", {"start": v(-3.92, 37.22) * mm, "end": v(-4.83, 40) * mm});
            skLineSegment(sketch, "E19.8", {"start": v(-4.83, 40) * mm, "end": v(-3.92, 42.78) * mm});
            skLineSegment(sketch, "E19.9", {"start": v(-3.92, 42.78) * mm, "end": v(-1.56, 44.5) * mm});
            skPoint(sketch, "E19.0.midPoint", {"position": v(-0.1, 44.5) * mm});
            skCircle(sketch, "E20.cCircle", {"center": v(-7.6, 53) * mm, "radius": 4.5 * mm, "construction": true});
            skLineSegment(sketch, "E20.0", {"start": v(-9.06, 57.5) * mm, "end": v(-6.13, 57.5) * mm});
            skLineSegment(sketch, "E20.1", {"start": v(-6.13, 57.5) * mm, "end": v(-3.77, 55.77) * mm});
            skLineSegment(sketch, "E20.2", {"start": v(-3.77, 55.77) * mm, "end": v(-2.86, 53) * mm});
            skLineSegment(sketch, "E20.3", {"start": v(-2.86, 53) * mm, "end": v(-3.77, 50.2) * mm});
            skLineSegment(sketch, "E20.4", {"start": v(-3.77, 50.2) * mm, "end": v(-6.13, 48.5) * mm});
            skLineSegment(sketch, "E20.5", {"start": v(-6.13, 48.5) * mm, "end": v(-9.06, 48.5) * mm});
            skLineSegment(sketch, "E20.6", {"start": v(-9.06, 48.5) * mm, "end": v(-11.42, 50.2) * mm});
            skLineSegment(sketch, "E20.7", {"start": v(-11.42, 50.2) * mm, "end": v(-12.33, 53) * mm});
            skLineSegment(sketch, "E20.8", {"start": v(-12.33, 53) * mm, "end": v(-11.42, 55.77) * mm});
            skLineSegment(sketch, "E20.9", {"start": v(-11.42, 55.77) * mm, "end": v(-9.06, 57.5) * mm});
            skPoint(sketch, "E20.0.midPoint", {"position": v(-7.6, 57.5) * mm});
            skCircle(sketch, "E21.cCircle", {"center": v(7.4, 53) * mm, "radius": 4.5 * mm, "construction": true});
            skLineSegment(sketch, "E21.0", {"start": v(5.94, 57.5) * mm, "end": v(8.87, 57.5) * mm});
            skLineSegment(sketch, "E21.1", {"start": v(8.87, 57.5) * mm, "end": v(11.23, 55.77) * mm});
            skLineSegment(sketch, "E21.2", {"start": v(11.23, 55.77) * mm, "end": v(12.14, 53) * mm});
            skLineSegment(sketch, "E21.3", {"start": v(12.14, 53) * mm, "end": v(11.23, 50.2) * mm});
            skLineSegment(sketch, "E21.4", {"start": v(11.23, 50.2) * mm, "end": v(8.87, 48.5) * mm});
            skLineSegment(sketch, "E21.5", {"start": v(8.87, 48.5) * mm, "end": v(5.94, 48.5) * mm});
            skLineSegment(sketch, "E21.6", {"start": v(5.94, 48.5) * mm, "end": v(3.58, 50.2) * mm});
            skLineSegment(sketch, "E21.7", {"start": v(3.58, 50.2) * mm, "end": v(2.67, 53) * mm});
            skLineSegment(sketch, "E21.8", {"start": v(2.67, 53) * mm, "end": v(3.58, 55.77) * mm});
            skLineSegment(sketch, "E21.9", {"start": v(3.58, 55.77) * mm, "end": v(5.94, 57.5) * mm});
            skPoint(sketch, "E21.0.midPoint", {"position": v(7.4, 57.5) * mm});
            skLineSegment(sketch, "E22", {"start": v(7.4, 53) * mm, "end": v(-7.6, 53) * mm, "construction": true});
            skLineSegment(sketch, "E23", {"start": v(-0.1, 40) * mm, "end": v(-7.6, 53) * mm, "construction": true});
            skLineSegment(sketch, "E24", {"start": v(-0.1, 40) * mm, "end": v(7.4, 53) * mm, "construction": true});
            skLineSegment(sketch, "E25", {"start": v(-0.07, 74.8) * mm, "end": v(0, 152.4) * mm, "construction": true});
            skLineSegment(sketch, "E26.direction1", {"start": v(-3.92, 37.22) * mm, "end": v(21.08, 37.22) * mm, "construction": true});
            skLineSegment(sketch, "E26.direction2", {"start": v(-3.92, 37.22) * mm, "end": v(-3.92, 67.22) * mm, "construction": true});
            skPoint(sketch, "E27.0.0.1", {"position": v(-0.1, 74.5) * mm});
            skLineSegment(sketch, "E27.1.0.1", {"start": v(-0.1, 70) * mm, "end": v(7.4, 83) * mm, "construction": true});
            skLineSegment(sketch, "E27.4.0.1", {"start": v(-0.1, 70) * mm, "end": v(-7.6, 83) * mm, "construction": true});
            skLineSegment(sketch, "E27.7.0.1", {"start": v(7.4, 83) * mm, "end": v(-7.6, 83) * mm, "construction": true});
            skPoint(sketch, "E27.10.0.1", {"position": v(7.4, 87.5) * mm});
            skPoint(sketch, "E27.11.0.1", {"position": v(-7.6, 87.5) * mm});
            skLineSegment(sketch, "E27.12.0.1", {"start": v(-3.77, 85.77) * mm, "end": v(-2.86, 83) * mm});
            skLineSegment(sketch, "E27.15.0.1", {"start": v(12.14, 83) * mm, "end": v(11.23, 80.2) * mm});
            skLineSegment(sketch, "E27.18.0.1", {"start": v(3.58, 85.77) * mm, "end": v(5.94, 87.5) * mm});
            skCircle(sketch, "E27.21.0.1", {"center": v(7.4, 83) * mm, "radius": 4.5 * mm, "construction": true});
            skLineSegment(sketch, "E27.23.0.1", {"start": v(3.58, 80.2) * mm, "end": v(2.67, 83) * mm});
            skLineSegment(sketch, "E27.26.0.1", {"start": v(-4.83, 70) * mm, "end": v(-3.92, 72.78) * mm});
            skLineSegment(sketch, "E27.29.0.1", {"start": v(3.73, 72.78) * mm, "end": v(4.64, 70) * mm});
            skLineSegment(sketch, "E27.32.0.1", {"start": v(-9.06, 78.5) * mm, "end": v(-11.42, 80.2) * mm});
            skLineSegment(sketch, "E27.35.0.1", {"start": v(1.37, 74.5) * mm, "end": v(3.73, 72.78) * mm});
            skLineSegment(sketch, "E27.38.0.1", {"start": v(-3.77, 80.2) * mm, "end": v(-6.13, 78.5) * mm});
            skLineSegment(sketch, "E27.41.0.1", {"start": v(-9.06, 87.5) * mm, "end": v(-6.13, 87.5) * mm});
            skLineSegment(sketch, "E27.44.0.1", {"start": v(-6.13, 87.5) * mm, "end": v(-3.77, 85.77) * mm});
            skCircle(sketch, "E27.47.0.1", {"center": v(-7.6, 83) * mm, "radius": 4.5 * mm, "construction": true});
            skLineSegment(sketch, "E27.49.0.1", {"start": v(11.23, 80.2) * mm, "end": v(8.87, 78.5) * mm});
            skLineSegment(sketch, "E27.52.0.1", {"start": v(-11.42, 85.77) * mm, "end": v(-9.06, 87.5) * mm});
            skLineSegment(sketch, "E27.55.0.1", {"start": v(11.23, 85.77) * mm, "end": v(12.14, 83) * mm});
            skLineSegment(sketch, "E27.58.0.1", {"start": v(-3.92, 67.22) * mm, "end": v(-4.83, 70) * mm});
            skLineSegment(sketch, "E27.61.0.1", {"start": v(-12.33, 83) * mm, "end": v(-11.42, 85.77) * mm});
            skLineSegment(sketch, "E27.64.0.1", {"start": v(8.87, 78.5) * mm, "end": v(5.94, 78.5) * mm});
            skLineSegment(sketch, "E27.67.0.1", {"start": v(-3.92, 72.78) * mm, "end": v(-1.56, 74.5) * mm});
            skLineSegment(sketch, "E27.70.0.1", {"start": v(-11.42, 80.2) * mm, "end": v(-12.33, 83) * mm});
            skLineSegment(sketch, "E27.73.0.1", {"start": v(-1.56, 65.5) * mm, "end": v(-3.92, 67.22) * mm});
            skLineSegment(sketch, "E27.76.0.1", {"start": v(5.94, 78.5) * mm, "end": v(3.58, 80.2) * mm});
            skCircle(sketch, "E27.79.0.1", {"center": v(-0.1, 70) * mm, "radius": 4.5 * mm, "construction": true});
            skLineSegment(sketch, "E27.81.0.1", {"start": v(-2.86, 83) * mm, "end": v(-3.77, 80.2) * mm});
            skLineSegment(sketch, "E27.84.0.1", {"start": v(2.67, 83) * mm, "end": v(3.58, 85.77) * mm});
            skLineSegment(sketch, "E27.87.0.1", {"start": v(8.87, 87.5) * mm, "end": v(11.23, 85.77) * mm});
            skLineSegment(sketch, "E27.90.0.1", {"start": v(4.64, 70) * mm, "end": v(3.73, 67.22) * mm});
            skLineSegment(sketch, "E27.93.0.1", {"start": v(3.73, 67.22) * mm, "end": v(1.37, 65.5) * mm});
            skLineSegment(sketch, "E27.96.0.1", {"start": v(5.94, 87.5) * mm, "end": v(8.87, 87.5) * mm});
            skLineSegment(sketch, "E27.99.0.1", {"start": v(-6.13, 78.5) * mm, "end": v(-9.06, 78.5) * mm});
            skLineSegment(sketch, "E27.102.0.1", {"start": v(1.37, 65.5) * mm, "end": v(-1.56, 65.5) * mm});
            skLineSegment(sketch, "E27.105.0.1", {"start": v(-1.56, 74.5) * mm, "end": v(1.37, 74.5) * mm});
            skPoint(sketch, "E27.0.0.2", {"position": v(-0.1, 104.5) * mm});
            skLineSegment(sketch, "E27.1.0.2", {"start": v(-0.1, 100) * mm, "end": v(7.4, 113) * mm, "construction": true});
            skLineSegment(sketch, "E27.4.0.2", {"start": v(-0.1, 100) * mm, "end": v(-7.6, 113) * mm, "construction": true});
            skLineSegment(sketch, "E27.7.0.2", {"start": v(7.4, 113) * mm, "end": v(-7.6, 113) * mm, "construction": true});
            skPoint(sketch, "E27.10.0.2", {"position": v(7.4, 117.5) * mm});
            skPoint(sketch, "E27.11.0.2", {"position": v(-7.6, 117.5) * mm});
            skLineSegment(sketch, "E27.12.0.2", {"start": v(-3.77, 115.77) * mm, "end": v(-2.86, 113) * mm});
            skLineSegment(sketch, "E27.15.0.2", {"start": v(12.14, 113) * mm, "end": v(11.23, 110.2) * mm});
            skLineSegment(sketch, "E27.18.0.2", {"start": v(3.58, 115.77) * mm, "end": v(5.94, 117.5) * mm});
            skCircle(sketch, "E27.21.0.2", {"center": v(7.4, 113) * mm, "radius": 4.5 * mm, "construction": true});
            skLineSegment(sketch, "E27.23.0.2", {"start": v(3.58, 110.2) * mm, "end": v(2.67, 113) * mm});
            skLineSegment(sketch, "E27.26.0.2", {"start": v(-4.83, 100) * mm, "end": v(-3.92, 102.78) * mm});
            skLineSegment(sketch, "E27.29.0.2", {"start": v(3.73, 102.78) * mm, "end": v(4.64, 100) * mm});
            skLineSegment(sketch, "E27.32.0.2", {"start": v(-9.06, 108.5) * mm, "end": v(-11.42, 110.2) * mm});
            skLineSegment(sketch, "E27.35.0.2", {"start": v(1.37, 104.5) * mm, "end": v(3.73, 102.78) * mm});
            skLineSegment(sketch, "E27.38.0.2", {"start": v(-3.77, 110.2) * mm, "end": v(-6.13, 108.5) * mm});
            skLineSegment(sketch, "E27.41.0.2", {"start": v(-9.06, 117.5) * mm, "end": v(-6.13, 117.5) * mm});
            skLineSegment(sketch, "E27.44.0.2", {"start": v(-6.13, 117.5) * mm, "end": v(-3.77, 115.77) * mm});
            skCircle(sketch, "E27.47.0.2", {"center": v(-7.6, 113) * mm, "radius": 4.5 * mm, "construction": true});
            skLineSegment(sketch, "E27.49.0.2", {"start": v(11.23, 110.2) * mm, "end": v(8.87, 108.5) * mm});
            skLineSegment(sketch, "E27.52.0.2", {"start": v(-11.42, 115.77) * mm, "end": v(-9.06, 117.5) * mm});
            skLineSegment(sketch, "E27.55.0.2", {"start": v(11.23, 115.77) * mm, "end": v(12.14, 113) * mm});
            skLineSegment(sketch, "E27.58.0.2", {"start": v(-3.92, 97.22) * mm, "end": v(-4.83, 100) * mm});
            skLineSegment(sketch, "E27.61.0.2", {"start": v(-12.33, 113) * mm, "end": v(-11.42, 115.77) * mm});
            skLineSegment(sketch, "E27.64.0.2", {"start": v(8.87, 108.5) * mm, "end": v(5.94, 108.5) * mm});
            skLineSegment(sketch, "E27.67.0.2", {"start": v(-3.92, 102.78) * mm, "end": v(-1.56, 104.5) * mm});
            skLineSegment(sketch, "E27.70.0.2", {"start": v(-11.42, 110.2) * mm, "end": v(-12.33, 113) * mm});
            skLineSegment(sketch, "E27.73.0.2", {"start": v(-1.56, 95.5) * mm, "end": v(-3.92, 97.22) * mm});
            skLineSegment(sketch, "E27.76.0.2", {"start": v(5.94, 108.5) * mm, "end": v(3.58, 110.2) * mm});
            skCircle(sketch, "E27.79.0.2", {"center": v(-0.1, 100) * mm, "radius": 4.5 * mm, "construction": true});
            skLineSegment(sketch, "E27.81.0.2", {"start": v(-2.86, 113) * mm, "end": v(-3.77, 110.2) * mm});
            skLineSegment(sketch, "E27.84.0.2", {"start": v(2.67, 113) * mm, "end": v(3.58, 115.77) * mm});
            skLineSegment(sketch, "E27.87.0.2", {"start": v(8.87, 117.5) * mm, "end": v(11.23, 115.77) * mm});
            skLineSegment(sketch, "E27.90.0.2", {"start": v(4.64, 100) * mm, "end": v(3.73, 97.22) * mm});
            skLineSegment(sketch, "E27.93.0.2", {"start": v(3.73, 97.22) * mm, "end": v(1.37, 95.5) * mm});
            skLineSegment(sketch, "E27.96.0.2", {"start": v(5.94, 117.5) * mm, "end": v(8.87, 117.5) * mm});
            skLineSegment(sketch, "E27.99.0.2", {"start": v(-6.13, 108.5) * mm, "end": v(-9.06, 108.5) * mm});
            skLineSegment(sketch, "E27.102.0.2", {"start": v(1.37, 95.5) * mm, "end": v(-1.56, 95.5) * mm});
            skLineSegment(sketch, "E27.105.0.2", {"start": v(-1.56, 104.5) * mm, "end": v(1.37, 104.5) * mm});
            skSolve(sketch);
        }
        {
            var Q0;
            Q0=makeQuery(id+"F1.opExtrude","SWEPT_FACE",FACE,{"disambiguationData":[OSD([sQuery(id+"F0.wireOp",EDGE,"E1.7")])]});
            var sketch = newSketch(context, id + "F5", { "sketchPlane" : qUnion([Q0])});
            skCircle(sketch, "E28.cCircle", {"center": v(0, 40) * mm, "radius": 4 * mm, "construction": true});
            skLineSegment(sketch, "E28.0", {"start": v(-1.3, 44) * mm, "end": v(1.3, 44) * mm});
            skLineSegment(sketch, "E28.1", {"start": v(1.3, 44) * mm, "end": v(3.4, 42.47) * mm});
            skLineSegment(sketch, "E28.2", {"start": v(3.4, 42.47) * mm, "end": v(4.2, 40) * mm});
            skLineSegment(sketch, "E28.3", {"start": v(4.2, 40) * mm, "end": v(3.4, 37.53) * mm});
            skLineSegment(sketch, "E28.4", {"start": v(3.4, 37.53) * mm, "end": v(1.3, 36) * mm});
            skLineSegment(sketch, "E28.5", {"start": v(1.3, 36) * mm, "end": v(-1.3, 36) * mm});
            skLineSegment(sketch, "E28.6", {"start": v(-1.3, 36) * mm, "end": v(-3.4, 37.53) * mm});
            skLineSegment(sketch, "E28.7", {"start": v(-3.4, 37.53) * mm, "end": v(-4.2, 40) * mm});
            skLineSegment(sketch, "E28.8", {"start": v(-4.2, 40) * mm, "end": v(-3.4, 42.47) * mm});
            skLineSegment(sketch, "E28.9", {"start": v(-3.4, 42.47) * mm, "end": v(-1.3, 44) * mm});
            skPoint(sketch, "E28.0.midPoint", {"position": v(0, 44) * mm});
            skCircle(sketch, "E29.cCircle", {"center": v(-7.5, 53) * mm, "radius": 4 * mm, "construction": true});
            skLineSegment(sketch, "E29.0", {"start": v(-8.8, 57) * mm, "end": v(-6.2, 57) * mm});
            skLineSegment(sketch, "E29.1", {"start": v(-6.2, 57) * mm, "end": v(-4.1, 55.46) * mm});
            skLineSegment(sketch, "E29.2", {"start": v(-4.1, 55.46) * mm, "end": v(-3.3, 53) * mm});
            skLineSegment(sketch, "E29.3", {"start": v(-3.3, 53) * mm, "end": v(-4.1, 50.52) * mm});
            skLineSegment(sketch, "E29.4", {"start": v(-4.1, 50.52) * mm, "end": v(-6.2, 49) * mm});
            skLineSegment(sketch, "E29.5", {"start": v(-6.2, 49) * mm, "end": v(-8.8, 49) * mm});
            skLineSegment(sketch, "E29.6", {"start": v(-8.8, 49) * mm, "end": v(-10.9, 50.52) * mm});
            skLineSegment(sketch, "E29.7", {"start": v(-10.9, 50.52) * mm, "end": v(-11.7, 53) * mm});
            skLineSegment(sketch, "E29.8", {"start": v(-11.7, 53) * mm, "end": v(-10.9, 55.46) * mm});
            skLineSegment(sketch, "E29.9", {"start": v(-10.9, 55.46) * mm, "end": v(-8.8, 57) * mm});
            skPoint(sketch, "E29.0.midPoint", {"position": v(-7.5, 57) * mm});
            skCircle(sketch, "E30.cCircle", {"center": v(7.5, 53) * mm, "radius": 4 * mm, "construction": true});
            skLineSegment(sketch, "E30.0", {"start": v(6.2, 57) * mm, "end": v(8.8, 57) * mm});
            skLineSegment(sketch, "E30.1", {"start": v(8.8, 57) * mm, "end": v(10.9, 55.46) * mm});
            skLineSegment(sketch, "E30.2", {"start": v(10.9, 55.46) * mm, "end": v(11.7, 53) * mm});
            skLineSegment(sketch, "E30.3", {"start": v(11.7, 53) * mm, "end": v(10.9, 50.52) * mm});
            skLineSegment(sketch, "E30.4", {"start": v(10.9, 50.52) * mm, "end": v(8.8, 49) * mm});
            skLineSegment(sketch, "E30.5", {"start": v(8.8, 49) * mm, "end": v(6.2, 49) * mm});
            skLineSegment(sketch, "E30.6", {"start": v(6.2, 49) * mm, "end": v(4.1, 50.52) * mm});
            skLineSegment(sketch, "E30.7", {"start": v(4.1, 50.52) * mm, "end": v(3.3, 53) * mm});
            skLineSegment(sketch, "E30.8", {"start": v(3.3, 53) * mm, "end": v(4.1, 55.46) * mm});
            skLineSegment(sketch, "E30.9", {"start": v(4.1, 55.46) * mm, "end": v(6.2, 57) * mm});
            skPoint(sketch, "E30.0.midPoint", {"position": v(7.5, 57) * mm});
            skLineSegment(sketch, "E31", {"start": v(7.5, 53) * mm, "end": v(-7.5, 53) * mm, "construction": true});
            skLineSegment(sketch, "E32", {"start": v(0, 40) * mm, "end": v(-7.5, 53) * mm, "construction": true});
            skLineSegment(sketch, "E33", {"start": v(0, 40) * mm, "end": v(7.5, 53) * mm, "construction": true});
            skLineSegment(sketch, "E34", {"start": v(0, 0) * mm, "end": v(0, 152.4) * mm, "construction": true});
            skLineSegment(sketch, "E35.direction1", {"start": v(-3.4, 37.53) * mm, "end": v(21.6, 37.53) * mm, "construction": true});
            skLineSegment(sketch, "E35.direction2", {"start": v(-3.4, 37.53) * mm, "end": v(-3.4, 67.53) * mm, "construction": true});
            skPoint(sketch, "E36.0.0.1", {"position": v(0, 74) * mm});
            skLineSegment(sketch, "E36.1.0.1", {"start": v(0, 70) * mm, "end": v(7.5, 83) * mm, "construction": true});
            skLineSegment(sketch, "E36.4.0.1", {"start": v(0, 70) * mm, "end": v(-7.5, 83) * mm, "construction": true});
            skLineSegment(sketch, "E36.7.0.1", {"start": v(7.5, 83) * mm, "end": v(-7.5, 83) * mm, "construction": true});
            skPoint(sketch, "E36.10.0.1", {"position": v(7.5, 87) * mm});
            skPoint(sketch, "E36.11.0.1", {"position": v(-7.5, 87) * mm});
            skLineSegment(sketch, "E36.12.0.1", {"start": v(-4.1, 85.46) * mm, "end": v(-3.3, 83) * mm});
            skLineSegment(sketch, "E36.15.0.1", {"start": v(11.7, 83) * mm, "end": v(10.9, 80.52) * mm});
            skLineSegment(sketch, "E36.18.0.1", {"start": v(4.1, 85.46) * mm, "end": v(6.2, 87) * mm});
            skCircle(sketch, "E36.21.0.1", {"center": v(7.5, 83) * mm, "radius": 4 * mm, "construction": true});
            skLineSegment(sketch, "E36.23.0.1", {"start": v(4.1, 80.52) * mm, "end": v(3.3, 83) * mm});
            skLineSegment(sketch, "E36.26.0.1", {"start": v(-4.2, 70) * mm, "end": v(-3.4, 72.47) * mm});
            skLineSegment(sketch, "E36.29.0.1", {"start": v(3.4, 72.47) * mm, "end": v(4.2, 70) * mm});
            skLineSegment(sketch, "E36.32.0.1", {"start": v(-8.8, 79) * mm, "end": v(-10.9, 80.52) * mm});
            skLineSegment(sketch, "E36.35.0.1", {"start": v(1.3, 74) * mm, "end": v(3.4, 72.47) * mm});
            skLineSegment(sketch, "E36.38.0.1", {"start": v(-4.1, 80.52) * mm, "end": v(-6.2, 79) * mm});
            skLineSegment(sketch, "E36.41.0.1", {"start": v(-8.8, 87) * mm, "end": v(-6.2, 87) * mm});
            skLineSegment(sketch, "E36.44.0.1", {"start": v(-6.2, 87) * mm, "end": v(-4.1, 85.46) * mm});
            skCircle(sketch, "E36.47.0.1", {"center": v(-7.5, 83) * mm, "radius": 4 * mm, "construction": true});
            skLineSegment(sketch, "E36.49.0.1", {"start": v(10.9, 80.52) * mm, "end": v(8.8, 79) * mm});
            skLineSegment(sketch, "E36.52.0.1", {"start": v(-10.9, 85.46) * mm, "end": v(-8.8, 87) * mm});
            skLineSegment(sketch, "E36.55.0.1", {"start": v(10.9, 85.46) * mm, "end": v(11.7, 83) * mm});
            skLineSegment(sketch, "E36.58.0.1", {"start": v(-3.4, 67.53) * mm, "end": v(-4.2, 70) * mm});
            skLineSegment(sketch, "E36.61.0.1", {"start": v(-11.7, 83) * mm, "end": v(-10.9, 85.46) * mm});
            skLineSegment(sketch, "E36.64.0.1", {"start": v(8.8, 79) * mm, "end": v(6.2, 79) * mm});
            skLineSegment(sketch, "E36.67.0.1", {"start": v(-3.4, 72.47) * mm, "end": v(-1.3, 74) * mm});
            skLineSegment(sketch, "E36.70.0.1", {"start": v(-10.9, 80.52) * mm, "end": v(-11.7, 83) * mm});
            skLineSegment(sketch, "E36.73.0.1", {"start": v(-1.3, 66) * mm, "end": v(-3.4, 67.53) * mm});
            skLineSegment(sketch, "E36.76.0.1", {"start": v(6.2, 79) * mm, "end": v(4.1, 80.52) * mm});
            skCircle(sketch, "E36.79.0.1", {"center": v(0, 70) * mm, "radius": 4 * mm, "construction": true});
            skLineSegment(sketch, "E36.81.0.1", {"start": v(-3.3, 83) * mm, "end": v(-4.1, 80.52) * mm});
            skLineSegment(sketch, "E36.84.0.1", {"start": v(3.3, 83) * mm, "end": v(4.1, 85.46) * mm});
            skLineSegment(sketch, "E36.87.0.1", {"start": v(8.8, 87) * mm, "end": v(10.9, 85.46) * mm});
            skLineSegment(sketch, "E36.90.0.1", {"start": v(4.2, 70) * mm, "end": v(3.4, 67.53) * mm});
            skLineSegment(sketch, "E36.93.0.1", {"start": v(3.4, 67.53) * mm, "end": v(1.3, 66) * mm});
            skLineSegment(sketch, "E36.96.0.1", {"start": v(6.2, 87) * mm, "end": v(8.8, 87) * mm});
            skLineSegment(sketch, "E36.99.0.1", {"start": v(-6.2, 79) * mm, "end": v(-8.8, 79) * mm});
            skLineSegment(sketch, "E36.102.0.1", {"start": v(1.3, 66) * mm, "end": v(-1.3, 66) * mm});
            skLineSegment(sketch, "E36.105.0.1", {"start": v(-1.3, 74) * mm, "end": v(1.3, 74) * mm});
            skPoint(sketch, "E36.0.0.2", {"position": v(0, 104) * mm});
            skLineSegment(sketch, "E36.1.0.2", {"start": v(0, 100) * mm, "end": v(7.5, 113) * mm, "construction": true});
            skLineSegment(sketch, "E36.4.0.2", {"start": v(0, 100) * mm, "end": v(-7.5, 113) * mm, "construction": true});
            skLineSegment(sketch, "E36.7.0.2", {"start": v(7.5, 113) * mm, "end": v(-7.5, 113) * mm, "construction": true});
            skPoint(sketch, "E36.10.0.2", {"position": v(7.5, 117) * mm});
            skPoint(sketch, "E36.11.0.2", {"position": v(-7.5, 117) * mm});
            skLineSegment(sketch, "E36.12.0.2", {"start": v(-4.1, 115.46) * mm, "end": v(-3.3, 113) * mm});
            skLineSegment(sketch, "E36.15.0.2", {"start": v(11.7, 113) * mm, "end": v(10.9, 110.52) * mm});
            skLineSegment(sketch, "E36.18.0.2", {"start": v(4.1, 115.46) * mm, "end": v(6.2, 117) * mm});
            skCircle(sketch, "E36.21.0.2", {"center": v(7.5, 113) * mm, "radius": 4 * mm, "construction": true});
            skLineSegment(sketch, "E36.23.0.2", {"start": v(4.1, 110.52) * mm, "end": v(3.3, 113) * mm});
            skLineSegment(sketch, "E36.26.0.2", {"start": v(-4.2, 100) * mm, "end": v(-3.4, 102.47) * mm});
            skLineSegment(sketch, "E36.29.0.2", {"start": v(3.4, 102.47) * mm, "end": v(4.2, 100) * mm});
            skLineSegment(sketch, "E36.32.0.2", {"start": v(-8.8, 109) * mm, "end": v(-10.9, 110.52) * mm});
            skLineSegment(sketch, "E36.35.0.2", {"start": v(1.3, 104) * mm, "end": v(3.4, 102.47) * mm});
            skLineSegment(sketch, "E36.38.0.2", {"start": v(-4.1, 110.52) * mm, "end": v(-6.2, 109) * mm});
            skLineSegment(sketch, "E36.41.0.2", {"start": v(-8.8, 117) * mm, "end": v(-6.2, 117) * mm});
            skLineSegment(sketch, "E36.44.0.2", {"start": v(-6.2, 117) * mm, "end": v(-4.1, 115.46) * mm});
            skCircle(sketch, "E36.47.0.2", {"center": v(-7.5, 113) * mm, "radius": 4 * mm, "construction": true});
            skLineSegment(sketch, "E36.49.0.2", {"start": v(10.9, 110.52) * mm, "end": v(8.8, 109) * mm});
            skLineSegment(sketch, "E36.52.0.2", {"start": v(-10.9, 115.46) * mm, "end": v(-8.8, 117) * mm});
            skLineSegment(sketch, "E36.55.0.2", {"start": v(10.9, 115.46) * mm, "end": v(11.7, 113) * mm});
            skLineSegment(sketch, "E36.58.0.2", {"start": v(-3.4, 97.53) * mm, "end": v(-4.2, 100) * mm});
            skLineSegment(sketch, "E36.61.0.2", {"start": v(-11.7, 113) * mm, "end": v(-10.9, 115.46) * mm});
            skLineSegment(sketch, "E36.64.0.2", {"start": v(8.8, 109) * mm, "end": v(6.2, 109) * mm});
            skLineSegment(sketch, "E36.67.0.2", {"start": v(-3.4, 102.47) * mm, "end": v(-1.3, 104) * mm});
            skLineSegment(sketch, "E36.70.0.2", {"start": v(-10.9, 110.52) * mm, "end": v(-11.7, 113) * mm});
            skLineSegment(sketch, "E36.73.0.2", {"start": v(-1.3, 96) * mm, "end": v(-3.4, 97.53) * mm});
            skLineSegment(sketch, "E36.76.0.2", {"start": v(6.2, 109) * mm, "end": v(4.1, 110.52) * mm});
            skCircle(sketch, "E36.79.0.2", {"center": v(0, 100) * mm, "radius": 4 * mm, "construction": true});
            skLineSegment(sketch, "E36.81.0.2", {"start": v(-3.3, 113) * mm, "end": v(-4.1, 110.52) * mm});
            skLineSegment(sketch, "E36.84.0.2", {"start": v(3.3, 113) * mm, "end": v(4.1, 115.46) * mm});
            skLineSegment(sketch, "E36.87.0.2", {"start": v(8.8, 117) * mm, "end": v(10.9, 115.46) * mm});
            skLineSegment(sketch, "E36.90.0.2", {"start": v(4.2, 100) * mm, "end": v(3.4, 97.53) * mm});
            skLineSegment(sketch, "E36.93.0.2", {"start": v(3.4, 97.53) * mm, "end": v(1.3, 96) * mm});
            skLineSegment(sketch, "E36.96.0.2", {"start": v(6.2, 117) * mm, "end": v(8.8, 117) * mm});
            skLineSegment(sketch, "E36.99.0.2", {"start": v(-6.2, 109) * mm, "end": v(-8.8, 109) * mm});
            skLineSegment(sketch, "E36.102.0.2", {"start": v(1.3, 96) * mm, "end": v(-1.3, 96) * mm});
            skLineSegment(sketch, "E36.105.0.2", {"start": v(-1.3, 104) * mm, "end": v(1.3, 104) * mm});
            skSolve(sketch);
        }
        {
            var Q0;
            Q0=makeQuery(id+"F1.opExtrude","SWEPT_FACE",FACE,{"disambiguationData":[OSD([sQuery(id+"F0.wireOp",EDGE,"E1.6")])]});
            var sketch = newSketch(context, id + "F6", { "sketchPlane" : qUnion([Q0])});
            skCircle(sketch, "E37.cCircle", {"center": v(0, 40) * mm, "radius": 3.5 * mm, "construction": true});
            skLineSegment(sketch, "E37.0", {"start": v(-1.14, 43.5) * mm, "end": v(1.14, 43.5) * mm});
            skLineSegment(sketch, "E37.1", {"start": v(1.14, 43.5) * mm, "end": v(2.98, 42.16) * mm});
            skLineSegment(sketch, "E37.2", {"start": v(2.98, 42.16) * mm, "end": v(3.68, 40) * mm});
            skLineSegment(sketch, "E37.3", {"start": v(3.68, 40) * mm, "end": v(2.98, 37.84) * mm});
            skLineSegment(sketch, "E37.4", {"start": v(2.98, 37.84) * mm, "end": v(1.14, 36.5) * mm});
            skLineSegment(sketch, "E37.5", {"start": v(1.14, 36.5) * mm, "end": v(-1.14, 36.5) * mm});
            skLineSegment(sketch, "E37.6", {"start": v(-1.14, 36.5) * mm, "end": v(-2.98, 37.84) * mm});
            skLineSegment(sketch, "E37.7", {"start": v(-2.98, 37.84) * mm, "end": v(-3.68, 40) * mm});
            skLineSegment(sketch, "E37.8", {"start": v(-3.68, 40) * mm, "end": v(-2.98, 42.16) * mm});
            skLineSegment(sketch, "E37.9", {"start": v(-2.98, 42.16) * mm, "end": v(-1.14, 43.5) * mm});
            skPoint(sketch, "E37.0.midPoint", {"position": v(0, 43.5) * mm});
            skCircle(sketch, "E38.cCircle", {"center": v(-7.5, 53) * mm, "radius": 3.5 * mm, "construction": true});
            skLineSegment(sketch, "E38.0", {"start": v(-8.64, 56.5) * mm, "end": v(-6.36, 56.5) * mm});
            skLineSegment(sketch, "E38.1", {"start": v(-6.36, 56.5) * mm, "end": v(-4.52, 55.15) * mm});
            skLineSegment(sketch, "E38.2", {"start": v(-4.52, 55.15) * mm, "end": v(-3.82, 53) * mm});
            skLineSegment(sketch, "E38.3", {"start": v(-3.82, 53) * mm, "end": v(-4.52, 50.83) * mm});
            skLineSegment(sketch, "E38.4", {"start": v(-4.52, 50.83) * mm, "end": v(-6.36, 49.5) * mm});
            skLineSegment(sketch, "E38.5", {"start": v(-6.36, 49.5) * mm, "end": v(-8.64, 49.5) * mm});
            skLineSegment(sketch, "E38.6", {"start": v(-8.64, 49.5) * mm, "end": v(-10.48, 50.83) * mm});
            skLineSegment(sketch, "E38.7", {"start": v(-10.48, 50.83) * mm, "end": v(-11.18, 53) * mm});
            skLineSegment(sketch, "E38.8", {"start": v(-11.18, 53) * mm, "end": v(-10.48, 55.15) * mm});
            skLineSegment(sketch, "E38.9", {"start": v(-10.48, 55.15) * mm, "end": v(-8.64, 56.5) * mm});
            skPoint(sketch, "E38.0.midPoint", {"position": v(-7.5, 56.5) * mm});
            skCircle(sketch, "E39.cCircle", {"center": v(7.5, 53) * mm, "radius": 3.5 * mm, "construction": true});
            skLineSegment(sketch, "E39.0", {"start": v(6.36, 56.5) * mm, "end": v(8.64, 56.5) * mm});
            skLineSegment(sketch, "E39.1", {"start": v(8.64, 56.5) * mm, "end": v(10.48, 55.15) * mm});
            skLineSegment(sketch, "E39.2", {"start": v(10.48, 55.15) * mm, "end": v(11.18, 53) * mm});
            skLineSegment(sketch, "E39.3", {"start": v(11.18, 53) * mm, "end": v(10.48, 50.83) * mm});
            skLineSegment(sketch, "E39.4", {"start": v(10.48, 50.83) * mm, "end": v(8.64, 49.5) * mm});
            skLineSegment(sketch, "E39.5", {"start": v(8.64, 49.5) * mm, "end": v(6.36, 49.5) * mm});
            skLineSegment(sketch, "E39.6", {"start": v(6.36, 49.5) * mm, "end": v(4.52, 50.83) * mm});
            skLineSegment(sketch, "E39.7", {"start": v(4.52, 50.83) * mm, "end": v(3.82, 53) * mm});
            skLineSegment(sketch, "E39.8", {"start": v(3.82, 53) * mm, "end": v(4.52, 55.15) * mm});
            skLineSegment(sketch, "E39.9", {"start": v(4.52, 55.15) * mm, "end": v(6.36, 56.5) * mm});
            skPoint(sketch, "E39.0.midPoint", {"position": v(7.5, 56.5) * mm});
            skLineSegment(sketch, "E40", {"start": v(7.5, 53) * mm, "end": v(-7.5, 53) * mm, "construction": true});
            skLineSegment(sketch, "E41", {"start": v(0, 40) * mm, "end": v(-7.5, 53) * mm, "construction": true});
            skLineSegment(sketch, "E42", {"start": v(0, 40) * mm, "end": v(7.5, 53) * mm, "construction": true});
            skLineSegment(sketch, "E43", {"start": v(0, 0) * mm, "end": v(0, 152.4) * mm, "construction": true});
            skLineSegment(sketch, "E44.direction1", {"start": v(-2.98, 37.84) * mm, "end": v(22.02, 37.84) * mm, "construction": true});
            skLineSegment(sketch, "E44.direction2", {"start": v(-2.98, 37.84) * mm, "end": v(-2.98, 67.84) * mm, "construction": true});
            skPoint(sketch, "E45.0.0.1", {"position": v(0, 73.5) * mm});
            skLineSegment(sketch, "E45.1.0.1", {"start": v(0, 70) * mm, "end": v(7.5, 83) * mm, "construction": true});
            skLineSegment(sketch, "E45.4.0.1", {"start": v(0, 70) * mm, "end": v(-7.5, 83) * mm, "construction": true});
            skLineSegment(sketch, "E45.7.0.1", {"start": v(7.5, 83) * mm, "end": v(-7.5, 83) * mm, "construction": true});
            skPoint(sketch, "E45.10.0.1", {"position": v(7.5, 86.5) * mm});
            skPoint(sketch, "E45.11.0.1", {"position": v(-7.5, 86.5) * mm});
            skLineSegment(sketch, "E45.12.0.1", {"start": v(-4.52, 85.15) * mm, "end": v(-3.82, 83) * mm});
            skLineSegment(sketch, "E45.15.0.1", {"start": v(11.18, 83) * mm, "end": v(10.48, 80.83) * mm});
            skLineSegment(sketch, "E45.18.0.1", {"start": v(4.52, 85.15) * mm, "end": v(6.36, 86.5) * mm});
            skCircle(sketch, "E45.21.0.1", {"center": v(7.5, 83) * mm, "radius": 3.5 * mm, "construction": true});
            skLineSegment(sketch, "E45.23.0.1", {"start": v(4.52, 80.83) * mm, "end": v(3.82, 83) * mm});
            skLineSegment(sketch, "E45.26.0.1", {"start": v(-3.68, 70) * mm, "end": v(-2.98, 72.16) * mm});
            skLineSegment(sketch, "E45.29.0.1", {"start": v(2.98, 72.16) * mm, "end": v(3.68, 70) * mm});
            skLineSegment(sketch, "E45.32.0.1", {"start": v(-8.64, 79.5) * mm, "end": v(-10.48, 80.83) * mm});
            skLineSegment(sketch, "E45.35.0.1", {"start": v(1.14, 73.5) * mm, "end": v(2.98, 72.16) * mm});
            skLineSegment(sketch, "E45.38.0.1", {"start": v(-4.52, 80.83) * mm, "end": v(-6.36, 79.5) * mm});
            skLineSegment(sketch, "E45.41.0.1", {"start": v(-8.64, 86.5) * mm, "end": v(-6.36, 86.5) * mm});
            skLineSegment(sketch, "E45.44.0.1", {"start": v(-6.36, 86.5) * mm, "end": v(-4.52, 85.15) * mm});
            skCircle(sketch, "E45.47.0.1", {"center": v(-7.5, 83) * mm, "radius": 3.5 * mm, "construction": true});
            skLineSegment(sketch, "E45.49.0.1", {"start": v(10.48, 80.83) * mm, "end": v(8.64, 79.5) * mm});
            skLineSegment(sketch, "E45.52.0.1", {"start": v(-10.48, 85.15) * mm, "end": v(-8.64, 86.5) * mm});
            skLineSegment(sketch, "E45.55.0.1", {"start": v(10.48, 85.15) * mm, "end": v(11.18, 83) * mm});
            skLineSegment(sketch, "E45.58.0.1", {"start": v(-2.98, 67.84) * mm, "end": v(-3.68, 70) * mm});
            skLineSegment(sketch, "E45.61.0.1", {"start": v(-11.18, 83) * mm, "end": v(-10.48, 85.15) * mm});
            skLineSegment(sketch, "E45.64.0.1", {"start": v(8.64, 79.5) * mm, "end": v(6.36, 79.5) * mm});
            skLineSegment(sketch, "E45.67.0.1", {"start": v(-2.98, 72.16) * mm, "end": v(-1.14, 73.5) * mm});
            skLineSegment(sketch, "E45.70.0.1", {"start": v(-10.48, 80.83) * mm, "end": v(-11.18, 83) * mm});
            skLineSegment(sketch, "E45.73.0.1", {"start": v(-1.14, 66.5) * mm, "end": v(-2.98, 67.84) * mm});
            skLineSegment(sketch, "E45.76.0.1", {"start": v(6.36, 79.5) * mm, "end": v(4.52, 80.83) * mm});
            skCircle(sketch, "E45.79.0.1", {"center": v(0, 70) * mm, "radius": 3.5 * mm, "construction": true});
            skLineSegment(sketch, "E45.81.0.1", {"start": v(-3.82, 83) * mm, "end": v(-4.52, 80.83) * mm});
            skLineSegment(sketch, "E45.84.0.1", {"start": v(3.82, 83) * mm, "end": v(4.52, 85.15) * mm});
            skLineSegment(sketch, "E45.87.0.1", {"start": v(8.64, 86.5) * mm, "end": v(10.48, 85.15) * mm});
            skLineSegment(sketch, "E45.90.0.1", {"start": v(3.68, 70) * mm, "end": v(2.98, 67.84) * mm});
            skLineSegment(sketch, "E45.93.0.1", {"start": v(2.98, 67.84) * mm, "end": v(1.14, 66.5) * mm});
            skLineSegment(sketch, "E45.96.0.1", {"start": v(6.36, 86.5) * mm, "end": v(8.64, 86.5) * mm});
            skLineSegment(sketch, "E45.99.0.1", {"start": v(-6.36, 79.5) * mm, "end": v(-8.64, 79.5) * mm});
            skLineSegment(sketch, "E45.102.0.1", {"start": v(1.14, 66.5) * mm, "end": v(-1.14, 66.5) * mm});
            skLineSegment(sketch, "E45.105.0.1", {"start": v(-1.14, 73.5) * mm, "end": v(1.14, 73.5) * mm});
            skPoint(sketch, "E45.0.0.2", {"position": v(0, 103.5) * mm});
            skLineSegment(sketch, "E45.1.0.2", {"start": v(0, 100) * mm, "end": v(7.5, 113) * mm, "construction": true});
            skLineSegment(sketch, "E45.4.0.2", {"start": v(0, 100) * mm, "end": v(-7.5, 113) * mm, "construction": true});
            skLineSegment(sketch, "E45.7.0.2", {"start": v(7.5, 113) * mm, "end": v(-7.5, 113) * mm, "construction": true});
            skPoint(sketch, "E45.10.0.2", {"position": v(7.5, 116.5) * mm});
            skPoint(sketch, "E45.11.0.2", {"position": v(-7.5, 116.5) * mm});
            skLineSegment(sketch, "E45.12.0.2", {"start": v(-4.52, 115.15) * mm, "end": v(-3.82, 113) * mm});
            skLineSegment(sketch, "E45.15.0.2", {"start": v(11.18, 113) * mm, "end": v(10.48, 110.83) * mm});
            skLineSegment(sketch, "E45.18.0.2", {"start": v(4.52, 115.15) * mm, "end": v(6.36, 116.5) * mm});
            skCircle(sketch, "E45.21.0.2", {"center": v(7.5, 113) * mm, "radius": 3.5 * mm, "construction": true});
            skLineSegment(sketch, "E45.23.0.2", {"start": v(4.52, 110.83) * mm, "end": v(3.82, 113) * mm});
            skLineSegment(sketch, "E45.26.0.2", {"start": v(-3.68, 100) * mm, "end": v(-2.98, 102.16) * mm});
            skLineSegment(sketch, "E45.29.0.2", {"start": v(2.98, 102.16) * mm, "end": v(3.68, 100) * mm});
            skLineSegment(sketch, "E45.32.0.2", {"start": v(-8.64, 109.5) * mm, "end": v(-10.48, 110.83) * mm});
            skLineSegment(sketch, "E45.35.0.2", {"start": v(1.14, 103.5) * mm, "end": v(2.98, 102.16) * mm});
            skLineSegment(sketch, "E45.38.0.2", {"start": v(-4.52, 110.83) * mm, "end": v(-6.36, 109.5) * mm});
            skLineSegment(sketch, "E45.41.0.2", {"start": v(-8.64, 116.5) * mm, "end": v(-6.36, 116.5) * mm});
            skLineSegment(sketch, "E45.44.0.2", {"start": v(-6.36, 116.5) * mm, "end": v(-4.52, 115.15) * mm});
            skCircle(sketch, "E45.47.0.2", {"center": v(-7.5, 113) * mm, "radius": 3.5 * mm, "construction": true});
            skLineSegment(sketch, "E45.49.0.2", {"start": v(10.48, 110.83) * mm, "end": v(8.64, 109.5) * mm});
            skLineSegment(sketch, "E45.52.0.2", {"start": v(-10.48, 115.15) * mm, "end": v(-8.64, 116.5) * mm});
            skLineSegment(sketch, "E45.55.0.2", {"start": v(10.48, 115.15) * mm, "end": v(11.18, 113) * mm});
            skLineSegment(sketch, "E45.58.0.2", {"start": v(-2.98, 97.84) * mm, "end": v(-3.68, 100) * mm});
            skLineSegment(sketch, "E45.61.0.2", {"start": v(-11.18, 113) * mm, "end": v(-10.48, 115.15) * mm});
            skLineSegment(sketch, "E45.64.0.2", {"start": v(8.64, 109.5) * mm, "end": v(6.36, 109.5) * mm});
            skLineSegment(sketch, "E45.67.0.2", {"start": v(-2.98, 102.16) * mm, "end": v(-1.14, 103.5) * mm});
            skLineSegment(sketch, "E45.70.0.2", {"start": v(-10.48, 110.83) * mm, "end": v(-11.18, 113) * mm});
            skLineSegment(sketch, "E45.73.0.2", {"start": v(-1.14, 96.5) * mm, "end": v(-2.98, 97.84) * mm});
            skLineSegment(sketch, "E45.76.0.2", {"start": v(6.36, 109.5) * mm, "end": v(4.52, 110.83) * mm});
            skCircle(sketch, "E45.79.0.2", {"center": v(0, 100) * mm, "radius": 3.5 * mm, "construction": true});
            skLineSegment(sketch, "E45.81.0.2", {"start": v(-3.82, 113) * mm, "end": v(-4.52, 110.83) * mm});
            skLineSegment(sketch, "E45.84.0.2", {"start": v(3.82, 113) * mm, "end": v(4.52, 115.15) * mm});
            skLineSegment(sketch, "E45.87.0.2", {"start": v(8.64, 116.5) * mm, "end": v(10.48, 115.15) * mm});
            skLineSegment(sketch, "E45.90.0.2", {"start": v(3.68, 100) * mm, "end": v(2.98, 97.84) * mm});
            skLineSegment(sketch, "E45.93.0.2", {"start": v(2.98, 97.84) * mm, "end": v(1.14, 96.5) * mm});
            skLineSegment(sketch, "E45.96.0.2", {"start": v(6.36, 116.5) * mm, "end": v(8.64, 116.5) * mm});
            skLineSegment(sketch, "E45.99.0.2", {"start": v(-6.36, 109.5) * mm, "end": v(-8.64, 109.5) * mm});
            skLineSegment(sketch, "E45.102.0.2", {"start": v(1.14, 96.5) * mm, "end": v(-1.14, 96.5) * mm});
            skLineSegment(sketch, "E45.105.0.2", {"start": v(-1.14, 103.5) * mm, "end": v(1.14, 103.5) * mm});
            skSolve(sketch);
        }
        {
            var Q0;
            Q0=makeQuery(id+"F1.opExtrude","SWEPT_FACE",FACE,{"disambiguationData":[OSD([sQuery(id+"F0.wireOp",EDGE,"E1.2")])]});
            var sketch = newSketch(context, id + "F7", { "sketchPlane" : qUnion([Q0])});
            skCircle(sketch, "E46.cCircle", {"center": v(0, 40) * mm, "radius": 3 * mm, "construction": true});
            skLineSegment(sketch, "E46.0", {"start": v(-0.97, 43) * mm, "end": v(0.97, 43) * mm});
            skLineSegment(sketch, "E46.1", {"start": v(0.97, 43) * mm, "end": v(2.55, 41.85) * mm});
            skLineSegment(sketch, "E46.2", {"start": v(2.55, 41.85) * mm, "end": v(3.15, 40) * mm});
            skLineSegment(sketch, "E46.3", {"start": v(3.15, 40) * mm, "end": v(2.55, 38.15) * mm});
            skLineSegment(sketch, "E46.4", {"start": v(2.55, 38.15) * mm, "end": v(0.97, 37) * mm});
            skLineSegment(sketch, "E46.5", {"start": v(0.97, 37) * mm, "end": v(-0.97, 37) * mm});
            skLineSegment(sketch, "E46.6", {"start": v(-0.97, 37) * mm, "end": v(-2.55, 38.15) * mm});
            skLineSegment(sketch, "E46.7", {"start": v(-2.55, 38.15) * mm, "end": v(-3.15, 40) * mm});
            skLineSegment(sketch, "E46.8", {"start": v(-3.15, 40) * mm, "end": v(-2.55, 41.85) * mm});
            skLineSegment(sketch, "E46.9", {"start": v(-2.55, 41.85) * mm, "end": v(-0.97, 43) * mm});
            skPoint(sketch, "E46.0.midPoint", {"position": v(0, 43) * mm});
            skCircle(sketch, "E47.cCircle", {"center": v(-7.5, 53) * mm, "radius": 3 * mm, "construction": true});
            skLineSegment(sketch, "E47.0", {"start": v(-8.47, 56) * mm, "end": v(-6.53, 56) * mm});
            skLineSegment(sketch, "E47.1", {"start": v(-6.53, 56) * mm, "end": v(-4.95, 54.84) * mm});
            skLineSegment(sketch, "E47.2", {"start": v(-4.95, 54.84) * mm, "end": v(-4.35, 53) * mm});
            skLineSegment(sketch, "E47.3", {"start": v(-4.35, 53) * mm, "end": v(-4.95, 51.14) * mm});
            skLineSegment(sketch, "E47.4", {"start": v(-4.95, 51.14) * mm, "end": v(-6.53, 50) * mm});
            skLineSegment(sketch, "E47.5", {"start": v(-6.53, 50) * mm, "end": v(-8.47, 50) * mm});
            skLineSegment(sketch, "E47.6", {"start": v(-8.47, 50) * mm, "end": v(-10.05, 51.14) * mm});
            skLineSegment(sketch, "E47.7", {"start": v(-10.05, 51.14) * mm, "end": v(-10.65, 53) * mm});
            skLineSegment(sketch, "E47.8", {"start": v(-10.65, 53) * mm, "end": v(-10.05, 54.84) * mm});
            skLineSegment(sketch, "E47.9", {"start": v(-10.05, 54.84) * mm, "end": v(-8.47, 56) * mm});
            skPoint(sketch, "E47.0.midPoint", {"position": v(-7.5, 56) * mm});
            skCircle(sketch, "E48.cCircle", {"center": v(7.5, 53) * mm, "radius": 3 * mm, "construction": true});
            skLineSegment(sketch, "E48.0", {"start": v(6.53, 56) * mm, "end": v(8.47, 56) * mm});
            skLineSegment(sketch, "E48.1", {"start": v(8.47, 56) * mm, "end": v(10.05, 54.84) * mm});
            skLineSegment(sketch, "E48.2", {"start": v(10.05, 54.84) * mm, "end": v(10.65, 53) * mm});
            skLineSegment(sketch, "E48.3", {"start": v(10.65, 53) * mm, "end": v(10.05, 51.14) * mm});
            skLineSegment(sketch, "E48.4", {"start": v(10.05, 51.14) * mm, "end": v(8.47, 50) * mm});
            skLineSegment(sketch, "E48.5", {"start": v(8.47, 50) * mm, "end": v(6.53, 50) * mm});
            skLineSegment(sketch, "E48.6", {"start": v(6.53, 50) * mm, "end": v(4.95, 51.14) * mm});
            skLineSegment(sketch, "E48.7", {"start": v(4.95, 51.14) * mm, "end": v(4.35, 53) * mm});
            skLineSegment(sketch, "E48.8", {"start": v(4.35, 53) * mm, "end": v(4.95, 54.84) * mm});
            skLineSegment(sketch, "E48.9", {"start": v(4.95, 54.84) * mm, "end": v(6.53, 56) * mm});
            skPoint(sketch, "E48.0.midPoint", {"position": v(7.5, 56) * mm});
            skLineSegment(sketch, "E49", {"start": v(7.5, 53) * mm, "end": v(-7.5, 53) * mm, "construction": true});
            skLineSegment(sketch, "E50", {"start": v(0, 40) * mm, "end": v(-7.5, 53) * mm, "construction": true});
            skLineSegment(sketch, "E51", {"start": v(0, 40) * mm, "end": v(7.5, 53) * mm, "construction": true});
            skLineSegment(sketch, "E52", {"start": v(0, 0) * mm, "end": v(0, 152.4) * mm, "construction": true});
            skLineSegment(sketch, "E53.direction1", {"start": v(-2.55, 38.15) * mm, "end": v(22.45, 38.15) * mm, "construction": true});
            skLineSegment(sketch, "E53.direction2", {"start": v(-2.55, 38.15) * mm, "end": v(-2.55, 68.15) * mm, "construction": true});
            skPoint(sketch, "E54.0.0.1", {"position": v(0, 73) * mm});
            skLineSegment(sketch, "E54.1.0.1", {"start": v(0, 70) * mm, "end": v(7.5, 83) * mm, "construction": true});
            skLineSegment(sketch, "E54.4.0.1", {"start": v(0, 70) * mm, "end": v(-7.5, 83) * mm, "construction": true});
            skLineSegment(sketch, "E54.7.0.1", {"start": v(7.5, 83) * mm, "end": v(-7.5, 83) * mm, "construction": true});
            skPoint(sketch, "E54.10.0.1", {"position": v(7.5, 86) * mm});
            skPoint(sketch, "E54.11.0.1", {"position": v(-7.5, 86) * mm});
            skLineSegment(sketch, "E54.12.0.1", {"start": v(-4.95, 84.84) * mm, "end": v(-4.35, 83) * mm});
            skLineSegment(sketch, "E54.15.0.1", {"start": v(10.65, 83) * mm, "end": v(10.05, 81.14) * mm});
            skLineSegment(sketch, "E54.18.0.1", {"start": v(4.95, 84.84) * mm, "end": v(6.53, 86) * mm});
            skCircle(sketch, "E54.21.0.1", {"center": v(7.5, 83) * mm, "radius": 3 * mm, "construction": true});
            skLineSegment(sketch, "E54.23.0.1", {"start": v(4.95, 81.14) * mm, "end": v(4.35, 83) * mm});
            skLineSegment(sketch, "E54.26.0.1", {"start": v(-3.15, 70) * mm, "end": v(-2.55, 71.85) * mm});
            skLineSegment(sketch, "E54.29.0.1", {"start": v(2.55, 71.85) * mm, "end": v(3.15, 70) * mm});
            skLineSegment(sketch, "E54.32.0.1", {"start": v(-8.47, 80) * mm, "end": v(-10.05, 81.14) * mm});
            skLineSegment(sketch, "E54.35.0.1", {"start": v(0.97, 73) * mm, "end": v(2.55, 71.85) * mm});
            skLineSegment(sketch, "E54.38.0.1", {"start": v(-4.95, 81.14) * mm, "end": v(-6.53, 80) * mm});
            skLineSegment(sketch, "E54.41.0.1", {"start": v(-8.47, 86) * mm, "end": v(-6.53, 86) * mm});
            skLineSegment(sketch, "E54.44.0.1", {"start": v(-6.53, 86) * mm, "end": v(-4.95, 84.84) * mm});
            skCircle(sketch, "E54.47.0.1", {"center": v(-7.5, 83) * mm, "radius": 3 * mm, "construction": true});
            skLineSegment(sketch, "E54.49.0.1", {"start": v(10.05, 81.14) * mm, "end": v(8.47, 80) * mm});
            skLineSegment(sketch, "E54.52.0.1", {"start": v(-10.05, 84.84) * mm, "end": v(-8.47, 86) * mm});
            skLineSegment(sketch, "E54.55.0.1", {"start": v(10.05, 84.84) * mm, "end": v(10.65, 83) * mm});
            skLineSegment(sketch, "E54.58.0.1", {"start": v(-2.55, 68.15) * mm, "end": v(-3.15, 70) * mm});
            skLineSegment(sketch, "E54.61.0.1", {"start": v(-10.65, 83) * mm, "end": v(-10.05, 84.84) * mm});
            skLineSegment(sketch, "E54.64.0.1", {"start": v(8.47, 80) * mm, "end": v(6.53, 80) * mm});
            skLineSegment(sketch, "E54.67.0.1", {"start": v(-2.55, 71.85) * mm, "end": v(-0.97, 73) * mm});
            skLineSegment(sketch, "E54.70.0.1", {"start": v(-10.05, 81.14) * mm, "end": v(-10.65, 83) * mm});
            skLineSegment(sketch, "E54.73.0.1", {"start": v(-0.97, 67) * mm, "end": v(-2.55, 68.15) * mm});
            skLineSegment(sketch, "E54.76.0.1", {"start": v(6.53, 80) * mm, "end": v(4.95, 81.14) * mm});
            skCircle(sketch, "E54.79.0.1", {"center": v(0, 70) * mm, "radius": 3 * mm, "construction": true});
            skLineSegment(sketch, "E54.81.0.1", {"start": v(-4.35, 83) * mm, "end": v(-4.95, 81.14) * mm});
            skLineSegment(sketch, "E54.84.0.1", {"start": v(4.35, 83) * mm, "end": v(4.95, 84.84) * mm});
            skLineSegment(sketch, "E54.87.0.1", {"start": v(8.47, 86) * mm, "end": v(10.05, 84.84) * mm});
            skLineSegment(sketch, "E54.90.0.1", {"start": v(3.15, 70) * mm, "end": v(2.55, 68.15) * mm});
            skLineSegment(sketch, "E54.93.0.1", {"start": v(2.55, 68.15) * mm, "end": v(0.97, 67) * mm});
            skLineSegment(sketch, "E54.96.0.1", {"start": v(6.53, 86) * mm, "end": v(8.47, 86) * mm});
            skLineSegment(sketch, "E54.99.0.1", {"start": v(-6.53, 80) * mm, "end": v(-8.47, 80) * mm});
            skLineSegment(sketch, "E54.102.0.1", {"start": v(0.97, 67) * mm, "end": v(-0.97, 67) * mm});
            skLineSegment(sketch, "E54.105.0.1", {"start": v(-0.97, 73) * mm, "end": v(0.97, 73) * mm});
            skPoint(sketch, "E54.0.0.2", {"position": v(0, 103) * mm});
            skLineSegment(sketch, "E54.1.0.2", {"start": v(0, 100) * mm, "end": v(7.5, 113) * mm, "construction": true});
            skLineSegment(sketch, "E54.4.0.2", {"start": v(0, 100) * mm, "end": v(-7.5, 113) * mm, "construction": true});
            skLineSegment(sketch, "E54.7.0.2", {"start": v(7.5, 113) * mm, "end": v(-7.5, 113) * mm, "construction": true});
            skPoint(sketch, "E54.10.0.2", {"position": v(7.5, 116) * mm});
            skPoint(sketch, "E54.11.0.2", {"position": v(-7.5, 116) * mm});
            skLineSegment(sketch, "E54.12.0.2", {"start": v(-4.95, 114.84) * mm, "end": v(-4.35, 113) * mm});
            skLineSegment(sketch, "E54.15.0.2", {"start": v(10.65, 113) * mm, "end": v(10.05, 111.14) * mm});
            skLineSegment(sketch, "E54.18.0.2", {"start": v(4.95, 114.84) * mm, "end": v(6.53, 116) * mm});
            skCircle(sketch, "E54.21.0.2", {"center": v(7.5, 113) * mm, "radius": 3 * mm, "construction": true});
            skLineSegment(sketch, "E54.23.0.2", {"start": v(4.95, 111.14) * mm, "end": v(4.35, 113) * mm});
            skLineSegment(sketch, "E54.26.0.2", {"start": v(-3.15, 100) * mm, "end": v(-2.55, 101.85) * mm});
            skLineSegment(sketch, "E54.29.0.2", {"start": v(2.55, 101.85) * mm, "end": v(3.15, 100) * mm});
            skLineSegment(sketch, "E54.32.0.2", {"start": v(-8.47, 110) * mm, "end": v(-10.05, 111.14) * mm});
            skLineSegment(sketch, "E54.35.0.2", {"start": v(0.97, 103) * mm, "end": v(2.55, 101.85) * mm});
            skLineSegment(sketch, "E54.38.0.2", {"start": v(-4.95, 111.14) * mm, "end": v(-6.53, 110) * mm});
            skLineSegment(sketch, "E54.41.0.2", {"start": v(-8.47, 116) * mm, "end": v(-6.53, 116) * mm});
            skLineSegment(sketch, "E54.44.0.2", {"start": v(-6.53, 116) * mm, "end": v(-4.95, 114.84) * mm});
            skCircle(sketch, "E54.47.0.2", {"center": v(-7.5, 113) * mm, "radius": 3 * mm, "construction": true});
            skLineSegment(sketch, "E54.49.0.2", {"start": v(10.05, 111.14) * mm, "end": v(8.47, 110) * mm});
            skLineSegment(sketch, "E54.52.0.2", {"start": v(-10.05, 114.84) * mm, "end": v(-8.47, 116) * mm});
            skLineSegment(sketch, "E54.55.0.2", {"start": v(10.05, 114.84) * mm, "end": v(10.65, 113) * mm});
            skLineSegment(sketch, "E54.58.0.2", {"start": v(-2.55, 98.15) * mm, "end": v(-3.15, 100) * mm});
            skLineSegment(sketch, "E54.61.0.2", {"start": v(-10.65, 113) * mm, "end": v(-10.05, 114.84) * mm});
            skLineSegment(sketch, "E54.64.0.2", {"start": v(8.47, 110) * mm, "end": v(6.53, 110) * mm});
            skLineSegment(sketch, "E54.67.0.2", {"start": v(-2.55, 101.85) * mm, "end": v(-0.97, 103) * mm});
            skLineSegment(sketch, "E54.70.0.2", {"start": v(-10.05, 111.14) * mm, "end": v(-10.65, 113) * mm});
            skLineSegment(sketch, "E54.73.0.2", {"start": v(-0.97, 97) * mm, "end": v(-2.55, 98.15) * mm});
            skLineSegment(sketch, "E54.76.0.2", {"start": v(6.53, 110) * mm, "end": v(4.95, 111.14) * mm});
            skCircle(sketch, "E54.79.0.2", {"center": v(0, 100) * mm, "radius": 3 * mm, "construction": true});
            skLineSegment(sketch, "E54.81.0.2", {"start": v(-4.35, 113) * mm, "end": v(-4.95, 111.14) * mm});
            skLineSegment(sketch, "E54.84.0.2", {"start": v(4.35, 113) * mm, "end": v(4.95, 114.84) * mm});
            skLineSegment(sketch, "E54.87.0.2", {"start": v(8.47, 116) * mm, "end": v(10.05, 114.84) * mm});
            skLineSegment(sketch, "E54.90.0.2", {"start": v(3.15, 100) * mm, "end": v(2.55, 98.15) * mm});
            skLineSegment(sketch, "E54.93.0.2", {"start": v(2.55, 98.15) * mm, "end": v(0.97, 97) * mm});
            skLineSegment(sketch, "E54.96.0.2", {"start": v(6.53, 116) * mm, "end": v(8.47, 116) * mm});
            skLineSegment(sketch, "E54.99.0.2", {"start": v(-6.53, 110) * mm, "end": v(-8.47, 110) * mm});
            skLineSegment(sketch, "E54.102.0.2", {"start": v(0.97, 97) * mm, "end": v(-0.97, 97) * mm});
            skLineSegment(sketch, "E54.105.0.2", {"start": v(-0.97, 103) * mm, "end": v(0.97, 103) * mm});
            skSolve(sketch);
        }
        {
            var Q0;
            Q0=makeQuery(id+"F1.opExtrude","SWEPT_FACE",FACE,{"disambiguationData":[OSD([sQuery(id+"F0.wireOp",EDGE,"E1.0")])]});
            var sketch = newSketch(context, id + "F8", { "sketchPlane" : qUnion([Q0])});
            skCircle(sketch, "E55.cCircle", {"center": v(0, 40) * mm, "radius": 2 * mm, "construction": true});
            skLineSegment(sketch, "E55.0", {"start": v(-0.65, 42) * mm, "end": v(0.65, 42) * mm});
            skLineSegment(sketch, "E55.1", {"start": v(0.65, 42) * mm, "end": v(1.7, 41.24) * mm});
            skLineSegment(sketch, "E55.2", {"start": v(1.7, 41.24) * mm, "end": v(2.1, 40) * mm});
            skLineSegment(sketch, "E55.3", {"start": v(2.1, 40) * mm, "end": v(1.7, 38.76) * mm});
            skLineSegment(sketch, "E55.4", {"start": v(1.7, 38.76) * mm, "end": v(0.65, 38) * mm});
            skLineSegment(sketch, "E55.5", {"start": v(0.65, 38) * mm, "end": v(-0.65, 38) * mm});
            skLineSegment(sketch, "E55.6", {"start": v(-0.65, 38) * mm, "end": v(-1.7, 38.76) * mm});
            skLineSegment(sketch, "E55.7", {"start": v(-1.7, 38.76) * mm, "end": v(-2.1, 40) * mm});
            skLineSegment(sketch, "E55.8", {"start": v(-2.1, 40) * mm, "end": v(-1.7, 41.24) * mm});
            skLineSegment(sketch, "E55.9", {"start": v(-1.7, 41.24) * mm, "end": v(-0.65, 42) * mm});
            skPoint(sketch, "E55.0.midPoint", {"position": v(0, 42) * mm});
            skCircle(sketch, "E56.cCircle", {"center": v(-7.5, 53) * mm, "radius": 2 * mm, "construction": true});
            skLineSegment(sketch, "E56.0", {"start": v(-8.15, 55) * mm, "end": v(-6.85, 55) * mm});
            skLineSegment(sketch, "E56.1", {"start": v(-6.85, 55) * mm, "end": v(-5.8, 54.23) * mm});
            skLineSegment(sketch, "E56.2", {"start": v(-5.8, 54.23) * mm, "end": v(-5.4, 53) * mm});
            skLineSegment(sketch, "E56.3", {"start": v(-5.4, 53) * mm, "end": v(-5.8, 51.75) * mm});
            skLineSegment(sketch, "E56.4", {"start": v(-5.8, 51.75) * mm, "end": v(-6.85, 51) * mm});
            skLineSegment(sketch, "E56.5", {"start": v(-6.85, 51) * mm, "end": v(-8.15, 51) * mm});
            skLineSegment(sketch, "E56.6", {"start": v(-8.15, 51) * mm, "end": v(-9.2, 51.75) * mm});
            skLineSegment(sketch, "E56.7", {"start": v(-9.2, 51.75) * mm, "end": v(-9.6, 53) * mm});
            skLineSegment(sketch, "E56.8", {"start": v(-9.6, 53) * mm, "end": v(-9.2, 54.23) * mm});
            skLineSegment(sketch, "E56.9", {"start": v(-9.2, 54.23) * mm, "end": v(-8.15, 55) * mm});
            skPoint(sketch, "E56.0.midPoint", {"position": v(-7.5, 55) * mm});
            skCircle(sketch, "E57.cCircle", {"center": v(7.5, 53) * mm, "radius": 2 * mm, "construction": true});
            skLineSegment(sketch, "E57.0", {"start": v(6.85, 55) * mm, "end": v(8.15, 55) * mm});
            skLineSegment(sketch, "E57.1", {"start": v(8.15, 55) * mm, "end": v(9.2, 54.23) * mm});
            skLineSegment(sketch, "E57.2", {"start": v(9.2, 54.23) * mm, "end": v(9.6, 53) * mm});
            skLineSegment(sketch, "E57.3", {"start": v(9.6, 53) * mm, "end": v(9.2, 51.75) * mm});
            skLineSegment(sketch, "E57.4", {"start": v(9.2, 51.75) * mm, "end": v(8.15, 51) * mm});
            skLineSegment(sketch, "E57.5", {"start": v(8.15, 51) * mm, "end": v(6.85, 51) * mm});
            skLineSegment(sketch, "E57.6", {"start": v(6.85, 51) * mm, "end": v(5.8, 51.75) * mm});
            skLineSegment(sketch, "E57.7", {"start": v(5.8, 51.75) * mm, "end": v(5.4, 53) * mm});
            skLineSegment(sketch, "E57.8", {"start": v(5.4, 53) * mm, "end": v(5.8, 54.23) * mm});
            skLineSegment(sketch, "E57.9", {"start": v(5.8, 54.23) * mm, "end": v(6.85, 55) * mm});
            skPoint(sketch, "E57.0.midPoint", {"position": v(7.5, 55) * mm});
            skLineSegment(sketch, "E58", {"start": v(7.5, 53) * mm, "end": v(-7.5, 53) * mm, "construction": true});
            skLineSegment(sketch, "E59", {"start": v(0, 40) * mm, "end": v(-7.5, 53) * mm, "construction": true});
            skLineSegment(sketch, "E60", {"start": v(0, 40) * mm, "end": v(7.5, 53) * mm, "construction": true});
            skLineSegment(sketch, "E61", {"start": v(0, 0) * mm, "end": v(0, 152.4) * mm, "construction": true});
            skLineSegment(sketch, "E62.direction1", {"start": v(-1.7, 38.76) * mm, "end": v(23.3, 38.76) * mm, "construction": true});
            skLineSegment(sketch, "E62.direction2", {"start": v(-1.7, 38.76) * mm, "end": v(-1.7, 68.76) * mm, "construction": true});
            skPoint(sketch, "E63.0.0.1", {"position": v(0, 72) * mm});
            skLineSegment(sketch, "E63.1.0.1", {"start": v(0, 70) * mm, "end": v(7.5, 83) * mm, "construction": true});
            skLineSegment(sketch, "E63.4.0.1", {"start": v(0, 70) * mm, "end": v(-7.5, 83) * mm, "construction": true});
            skLineSegment(sketch, "E63.7.0.1", {"start": v(7.5, 83) * mm, "end": v(-7.5, 83) * mm, "construction": true});
            skPoint(sketch, "E63.10.0.1", {"position": v(7.5, 85) * mm});
            skPoint(sketch, "E63.11.0.1", {"position": v(-7.5, 85) * mm});
            skLineSegment(sketch, "E63.12.0.1", {"start": v(-5.8, 84.23) * mm, "end": v(-5.4, 83) * mm});
            skLineSegment(sketch, "E63.15.0.1", {"start": v(9.6, 83) * mm, "end": v(9.2, 81.75) * mm});
            skLineSegment(sketch, "E63.18.0.1", {"start": v(5.8, 84.23) * mm, "end": v(6.85, 85) * mm});
            skCircle(sketch, "E63.21.0.1", {"center": v(7.5, 83) * mm, "radius": 2 * mm, "construction": true});
            skLineSegment(sketch, "E63.23.0.1", {"start": v(5.8, 81.75) * mm, "end": v(5.4, 83) * mm});
            skLineSegment(sketch, "E63.26.0.1", {"start": v(-2.1, 70) * mm, "end": v(-1.7, 71.24) * mm});
            skLineSegment(sketch, "E63.29.0.1", {"start": v(1.7, 71.24) * mm, "end": v(2.1, 70) * mm});
            skLineSegment(sketch, "E63.32.0.1", {"start": v(-8.15, 81) * mm, "end": v(-9.2, 81.75) * mm});
            skLineSegment(sketch, "E63.35.0.1", {"start": v(0.65, 72) * mm, "end": v(1.7, 71.24) * mm});
            skLineSegment(sketch, "E63.38.0.1", {"start": v(-5.8, 81.75) * mm, "end": v(-6.85, 81) * mm});
            skLineSegment(sketch, "E63.41.0.1", {"start": v(-8.15, 85) * mm, "end": v(-6.85, 85) * mm});
            skLineSegment(sketch, "E63.44.0.1", {"start": v(-6.85, 85) * mm, "end": v(-5.8, 84.23) * mm});
            skCircle(sketch, "E63.47.0.1", {"center": v(-7.5, 83) * mm, "radius": 2 * mm, "construction": true});
            skLineSegment(sketch, "E63.49.0.1", {"start": v(9.2, 81.75) * mm, "end": v(8.15, 81) * mm});
            skLineSegment(sketch, "E63.52.0.1", {"start": v(-9.2, 84.23) * mm, "end": v(-8.15, 85) * mm});
            skLineSegment(sketch, "E63.55.0.1", {"start": v(9.2, 84.23) * mm, "end": v(9.6, 83) * mm});
            skLineSegment(sketch, "E63.58.0.1", {"start": v(-1.7, 68.76) * mm, "end": v(-2.1, 70) * mm});
            skLineSegment(sketch, "E63.61.0.1", {"start": v(-9.6, 83) * mm, "end": v(-9.2, 84.23) * mm});
            skLineSegment(sketch, "E63.64.0.1", {"start": v(8.15, 81) * mm, "end": v(6.85, 81) * mm});
            skLineSegment(sketch, "E63.67.0.1", {"start": v(-1.7, 71.24) * mm, "end": v(-0.65, 72) * mm});
            skLineSegment(sketch, "E63.70.0.1", {"start": v(-9.2, 81.75) * mm, "end": v(-9.6, 83) * mm});
            skLineSegment(sketch, "E63.73.0.1", {"start": v(-0.65, 68) * mm, "end": v(-1.7, 68.76) * mm});
            skLineSegment(sketch, "E63.76.0.1", {"start": v(6.85, 81) * mm, "end": v(5.8, 81.75) * mm});
            skCircle(sketch, "E63.79.0.1", {"center": v(0, 70) * mm, "radius": 2 * mm, "construction": true});
            skLineSegment(sketch, "E63.81.0.1", {"start": v(-5.4, 83) * mm, "end": v(-5.8, 81.75) * mm});
            skLineSegment(sketch, "E63.84.0.1", {"start": v(5.4, 83) * mm, "end": v(5.8, 84.23) * mm});
            skLineSegment(sketch, "E63.87.0.1", {"start": v(8.15, 85) * mm, "end": v(9.2, 84.23) * mm});
            skLineSegment(sketch, "E63.90.0.1", {"start": v(2.1, 70) * mm, "end": v(1.7, 68.76) * mm});
            skLineSegment(sketch, "E63.93.0.1", {"start": v(1.7, 68.76) * mm, "end": v(0.65, 68) * mm});
            skLineSegment(sketch, "E63.96.0.1", {"start": v(6.85, 85) * mm, "end": v(8.15, 85) * mm});
            skLineSegment(sketch, "E63.99.0.1", {"start": v(-6.85, 81) * mm, "end": v(-8.15, 81) * mm});
            skLineSegment(sketch, "E63.102.0.1", {"start": v(0.65, 68) * mm, "end": v(-0.65, 68) * mm});
            skLineSegment(sketch, "E63.105.0.1", {"start": v(-0.65, 72) * mm, "end": v(0.65, 72) * mm});
            skPoint(sketch, "E63.0.0.2", {"position": v(0, 102) * mm});
            skLineSegment(sketch, "E63.1.0.2", {"start": v(0, 100) * mm, "end": v(7.5, 113) * mm, "construction": true});
            skLineSegment(sketch, "E63.4.0.2", {"start": v(0, 100) * mm, "end": v(-7.5, 113) * mm, "construction": true});
            skLineSegment(sketch, "E63.7.0.2", {"start": v(7.5, 113) * mm, "end": v(-7.5, 113) * mm, "construction": true});
            skPoint(sketch, "E63.10.0.2", {"position": v(7.5, 115) * mm});
            skPoint(sketch, "E63.11.0.2", {"position": v(-7.5, 115) * mm});
            skLineSegment(sketch, "E63.12.0.2", {"start": v(-5.8, 114.23) * mm, "end": v(-5.4, 113) * mm});
            skLineSegment(sketch, "E63.15.0.2", {"start": v(9.6, 113) * mm, "end": v(9.2, 111.75) * mm});
            skLineSegment(sketch, "E63.18.0.2", {"start": v(5.8, 114.23) * mm, "end": v(6.85, 115) * mm});
            skCircle(sketch, "E63.21.0.2", {"center": v(7.5, 113) * mm, "radius": 2 * mm, "construction": true});
            skLineSegment(sketch, "E63.23.0.2", {"start": v(5.8, 111.75) * mm, "end": v(5.4, 113) * mm});
            skLineSegment(sketch, "E63.26.0.2", {"start": v(-2.1, 100) * mm, "end": v(-1.7, 101.24) * mm});
            skLineSegment(sketch, "E63.29.0.2", {"start": v(1.7, 101.24) * mm, "end": v(2.1, 100) * mm});
            skLineSegment(sketch, "E63.32.0.2", {"start": v(-8.15, 111) * mm, "end": v(-9.2, 111.75) * mm});
            skLineSegment(sketch, "E63.35.0.2", {"start": v(0.65, 102) * mm, "end": v(1.7, 101.24) * mm});
            skLineSegment(sketch, "E63.38.0.2", {"start": v(-5.8, 111.75) * mm, "end": v(-6.85, 111) * mm});
            skLineSegment(sketch, "E63.41.0.2", {"start": v(-8.15, 115) * mm, "end": v(-6.85, 115) * mm});
            skLineSegment(sketch, "E63.44.0.2", {"start": v(-6.85, 115) * mm, "end": v(-5.8, 114.23) * mm});
            skCircle(sketch, "E63.47.0.2", {"center": v(-7.5, 113) * mm, "radius": 2 * mm, "construction": true});
            skLineSegment(sketch, "E63.49.0.2", {"start": v(9.2, 111.75) * mm, "end": v(8.15, 111) * mm});
            skLineSegment(sketch, "E63.52.0.2", {"start": v(-9.2, 114.23) * mm, "end": v(-8.15, 115) * mm});
            skLineSegment(sketch, "E63.55.0.2", {"start": v(9.2, 114.23) * mm, "end": v(9.6, 113) * mm});
            skLineSegment(sketch, "E63.58.0.2", {"start": v(-1.7, 98.76) * mm, "end": v(-2.1, 100) * mm});
            skLineSegment(sketch, "E63.61.0.2", {"start": v(-9.6, 113) * mm, "end": v(-9.2, 114.23) * mm});
            skLineSegment(sketch, "E63.64.0.2", {"start": v(8.15, 111) * mm, "end": v(6.85, 111) * mm});
            skLineSegment(sketch, "E63.67.0.2", {"start": v(-1.7, 101.24) * mm, "end": v(-0.65, 102) * mm});
            skLineSegment(sketch, "E63.70.0.2", {"start": v(-9.2, 111.75) * mm, "end": v(-9.6, 113) * mm});
            skLineSegment(sketch, "E63.73.0.2", {"start": v(-0.65, 98) * mm, "end": v(-1.7, 98.76) * mm});
            skLineSegment(sketch, "E63.76.0.2", {"start": v(6.85, 111) * mm, "end": v(5.8, 111.75) * mm});
            skCircle(sketch, "E63.79.0.2", {"center": v(0, 100) * mm, "radius": 2 * mm, "construction": true});
            skLineSegment(sketch, "E63.81.0.2", {"start": v(-5.4, 113) * mm, "end": v(-5.8, 111.75) * mm});
            skLineSegment(sketch, "E63.84.0.2", {"start": v(5.4, 113) * mm, "end": v(5.8, 114.23) * mm});
            skLineSegment(sketch, "E63.87.0.2", {"start": v(8.15, 115) * mm, "end": v(9.2, 114.23) * mm});
            skLineSegment(sketch, "E63.90.0.2", {"start": v(2.1, 100) * mm, "end": v(1.7, 98.76) * mm});
            skLineSegment(sketch, "E63.93.0.2", {"start": v(1.7, 98.76) * mm, "end": v(0.65, 98) * mm});
            skLineSegment(sketch, "E63.96.0.2", {"start": v(6.85, 115) * mm, "end": v(8.15, 115) * mm});
            skLineSegment(sketch, "E63.99.0.2", {"start": v(-6.85, 111) * mm, "end": v(-8.15, 111) * mm});
            skLineSegment(sketch, "E63.102.0.2", {"start": v(0.65, 98) * mm, "end": v(-0.65, 98) * mm});
            skLineSegment(sketch, "E63.105.0.2", {"start": v(-0.65, 102) * mm, "end": v(0.65, 102) * mm});
            skSolve(sketch);
        }
        {
            var Q0;
            Q0 = qSketchRegion(id + "F8", true);
            extrude(context, id + "F9", {"entities" : qUnion([Q0]), "operationType" : NewBodyOperationType.REMOVE, "endBound" : BoundingType.UP_TO_NEXT, "oppositeDirection" : true, "depth" : 10 * mm});
        }
        {
            var Q0;
            Q0 = qSketchRegion(id + "F7", true);
            extrude(context, id + "F10", {"entities" : qUnion([Q0]), "operationType" : NewBodyOperationType.REMOVE, "endBound" : BoundingType.UP_TO_NEXT, "oppositeDirection" : true, "depth" : 25 * mm});
        }
        {
            var Q0;
            Q0 = qSketchRegion(id + "F6", true);
            extrude(context, id + "F11", {"entities" : qUnion([Q0]), "operationType" : NewBodyOperationType.REMOVE, "endBound" : BoundingType.UP_TO_NEXT, "oppositeDirection" : true, "depth" : 25 * mm});
        }
        {
            var Q0;
            Q0 = qSketchRegion(id + "F5", true);
            extrude(context, id + "F12", {"entities" : qUnion([Q0]), "operationType" : NewBodyOperationType.REMOVE, "endBound" : BoundingType.UP_TO_NEXT, "oppositeDirection" : true, "depth" : 25 * mm});
        }
        {
            var Q0;
            Q0 = qSketchRegion(id + "F4", true);
            extrude(context, id + "F13", {"entities" : qUnion([Q0]), "operationType" : NewBodyOperationType.REMOVE, "endBound" : BoundingType.UP_TO_NEXT, "oppositeDirection" : true, "depth" : 25 * mm});
        }
        {
            var Q0;
            Q0 = qSketchRegion(id + "F3", true);
            extrude(context, id + "F14", {"entities" : qUnion([Q0]), "operationType" : NewBodyOperationType.REMOVE, "endBound" : BoundingType.UP_TO_NEXT, "oppositeDirection" : true, "depth" : 25 * mm});
        }
        {
            var Q0;
            Q0 = qSketchRegion(id + "F2", true);
            extrude(context, id + "F15", {"entities" : qUnion([Q0]), "operationType" : NewBodyOperationType.REMOVE, "oppositeDirection" : true, "depth" : 25 * mm});
        }
        {
            var Q0;
            Q0=qCreatedBy(makeId("Top.planeOp"),FACE);
            var sketch = newSketch(context, id + "F16", { "sketchPlane" : qUnion([Q0])});
            skCircle(sketch, "E64", {"center": v(0, 0) * mm, "radius": 22.2 * mm});
            skCircle(sketch, "E65.0", {"center": v(0, 0) * mm, "radius": 25.6 * mm});
            skLineSegment(sketch, "E66.0", {"start": v(11.17, -52.23) * mm, "end": v(-21.67, -48.82) * mm, "construction": true});
            skLineSegment(sketch, "E67.0", {"start": v(-46.23, -26.76) * mm, "end": v(-53.13, 5.52) * mm, "construction": true});
            skLineSegment(sketch, "E68.0", {"start": v(-39.74, 35.7) * mm, "end": v(-11.17, 52.23) * mm, "construction": true});
            skLineSegment(sketch, "E69.0", {"start": v(21.67, 48.82) * mm, "end": v(46.23, 26.76) * mm, "construction": true});
            skLineSegment(sketch, "E70.0", {"start": v(53.13, -5.52) * mm, "end": v(39.74, -35.7) * mm, "construction": true});
            skLineSegment(sketch, "E71", {"start": v(-5.25, -50.53) * mm, "end": v(0, 0) * mm, "construction": true});
            skLineSegment(sketch, "E72", {"start": v(0, 0) * mm, "end": v(-49.68, -10.62) * mm, "construction": true});
            skLineSegment(sketch, "E73", {"start": v(0, 0) * mm, "end": v(-25.45, 43.96) * mm, "construction": true});
            skLineSegment(sketch, "E74", {"start": v(33.95, 37.8) * mm, "end": v(0, 0) * mm, "construction": true});
            skLineSegment(sketch, "E75", {"start": v(46.43, -20.6) * mm, "end": v(0, 0) * mm, "construction": true});
            skLineSegment(sketch, "E76.bottom", {"start": v(-7.25, -50.32) * mm, "end": v(-3.25, -50.74) * mm});
            skLineSegment(sketch, "E76.top", {"start": v(-4.3, -21.87) * mm, "end": v(-0.3, -22.29) * mm});
            skLineSegment(sketch, "E76.left", {"start": v(-7.25, -50.32) * mm, "end": v(-4.3, -21.87) * mm});
            skLineSegment(sketch, "E76.right", {"start": v(-3.25, -50.74) * mm, "end": v(-0.3, -22.29) * mm});
            skPoint(sketch, "E77", {"position": v(-5.25, -50.53) * mm});
            skPoint(sketch, "E78", {"position": v(-2.3, -22.08) * mm});
            skLineSegment(sketch, "E79.1.0", {"start": v(45.62, -22.44) * mm, "end": v(19.48, -10.84) * mm});
            skPoint(sketch, "E79.1.1", {"position": v(20.3, -9) * mm});
            skLineSegment(sketch, "E79.1.2", {"start": v(47.25, -18.77) * mm, "end": v(21.1, -7.17) * mm});
            skLineSegment(sketch, "E79.1.3", {"start": v(19.48, -10.84) * mm, "end": v(21.1, -7.17) * mm});
            skPoint(sketch, "E79.1.4", {"position": v(46.43, -20.6) * mm});
            skLineSegment(sketch, "E79.1.5", {"start": v(45.62, -22.44) * mm, "end": v(47.25, -18.77) * mm});
            skLineSegment(sketch, "E79.2.0", {"start": v(35.44, 36.45) * mm, "end": v(16.33, 15.17) * mm});
            skPoint(sketch, "E79.2.1", {"position": v(14.83, 16.52) * mm});
            skLineSegment(sketch, "E79.2.2", {"start": v(32.45, 39.13) * mm, "end": v(13.34, 17.86) * mm});
            skLineSegment(sketch, "E79.2.3", {"start": v(16.33, 15.17) * mm, "end": v(13.34, 17.86) * mm});
            skPoint(sketch, "E79.2.4", {"position": v(33.95, 37.8) * mm});
            skLineSegment(sketch, "E79.2.5", {"start": v(35.44, 36.45) * mm, "end": v(32.45, 39.13) * mm});
            skLineSegment(sketch, "E79.3.0", {"start": v(-23.72, 44.97) * mm, "end": v(-9.39, 20.22) * mm});
            skPoint(sketch, "E79.3.1", {"position": v(-11.12, 19.21) * mm});
            skLineSegment(sketch, "E79.3.2", {"start": v(-27.19, 42.96) * mm, "end": v(-12.86, 18.2) * mm});
            skLineSegment(sketch, "E79.3.3", {"start": v(-9.39, 20.22) * mm, "end": v(-12.86, 18.2) * mm});
            skPoint(sketch, "E79.3.4", {"position": v(-25.45, 43.96) * mm});
            skLineSegment(sketch, "E79.3.5", {"start": v(-23.72, 44.97) * mm, "end": v(-27.19, 42.96) * mm});
            skLineSegment(sketch, "E79.4.0", {"start": v(-50.1, -8.66) * mm, "end": v(-22.13, -2.68) * mm});
            skPoint(sketch, "E79.4.1", {"position": v(-21.7, -4.64) * mm});
            skLineSegment(sketch, "E79.4.2", {"start": v(-49.26, -12.58) * mm, "end": v(-21.29, -6.6) * mm});
            skLineSegment(sketch, "E79.4.3", {"start": v(-22.13, -2.68) * mm, "end": v(-21.29, -6.6) * mm});
            skPoint(sketch, "E79.4.4", {"position": v(-49.68, -10.62) * mm});
            skLineSegment(sketch, "E79.4.5", {"start": v(-50.1, -8.66) * mm, "end": v(-49.26, -12.58) * mm});
            skSolve(sketch);
        }
        {
            var Q0;
            {var subQ5=sQuery(id+"F16.wireOp",EDGE,"E79.4.5");Q0=makeQuery(id+"F16.imprint","IMPRINT",FACE,{"disambiguationData":[TD([[makeQuery(id+"F16.imprint","IMPRINT",EDGE,{"derivedFrom":subQ5}),1.0]])]});}
            var Q1;
            {var subQ5=sQuery(id+"F16.wireOp",EDGE,"E76.bottom");Q1=makeQuery(id+"F16.imprint","IMPRINT",FACE,{"disambiguationData":[TD([[makeQuery(id+"F16.imprint","IMPRINT",EDGE,{"derivedFrom":subQ5}),1.0]])]});}
            var Q2;
            {var subQ1=sQuery(id+"F16.wireOp",EDGE,"E76.top");var subQ5=sQuery(id+"F16.wireOp",EDGE,"E64");var subQ6=makeQuery(id+"F16.imprint","INTERSECT",VERTEX,{"derivedFrom":[subQ5,subQ1]});Q2=makeQuery(id+"F16.imprint","IMPRINT",FACE,{"disambiguationData":[TD([[makeQuery(id+"F16.imprint","IMPRINT",EDGE,{"disambiguationData":[TD([[subQ6,-1.0]])],"derivedFrom":subQ5}),-1.0]])]});}
            var Q3;
            {var subQ4=sQuery(id+"F16.wireOp",EDGE,"E76.left");var subQ6=sQuery(id+"F16.wireOp",EDGE,"E65.0");var subQ7=makeQuery(id+"F16.imprint","INTERSECT",VERTEX,{"derivedFrom":[subQ6,subQ4]});Q3=makeQuery(id+"F16.imprint","IMPRINT",FACE,{"disambiguationData":[TD([[makeQuery(id+"F16.imprint","IMPRINT",EDGE,{"disambiguationData":[TD([[subQ7,-1.0]])],"derivedFrom":subQ6}),1.0]])]});}
            var Q4;
            {var subQ7=sQuery(id+"F16.wireOp",EDGE,"E64");var subQ9=sQuery(id+"F16.wireOp",EDGE,"E79.4.3");var subQ10=makeQuery(id+"F16.imprint","INTERSECT",VERTEX,{"derivedFrom":[subQ7,subQ9]});Q4=makeQuery(id+"F16.imprint","IMPRINT",FACE,{"disambiguationData":[TD([[makeQuery(id+"F16.imprint","IMPRINT",EDGE,{"disambiguationData":[TD([[subQ10,-1.0]])],"derivedFrom":subQ7}),-1.0]])]});}
            var Q5;
            {var subQ1=sQuery(id+"F16.wireOp",EDGE,"E79.4.0");var subQ6=sQuery(id+"F16.wireOp",EDGE,"E65.0");var subQ8=makeQuery(id+"F16.imprint","INTERSECT",VERTEX,{"derivedFrom":[subQ6,subQ1]});Q5=makeQuery(id+"F16.imprint","IMPRINT",FACE,{"disambiguationData":[TD([[makeQuery(id+"F16.imprint","IMPRINT",EDGE,{"disambiguationData":[TD([[subQ8,-1.0]])],"derivedFrom":subQ6}),1.0]])]});}
            var Q6;
            {var subQ0=sQuery(id+"F16.wireOp",EDGE,"E79.3.3");var subQ3=sQuery(id+"F16.wireOp",EDGE,"E64");var subQ4=makeQuery(id+"F16.imprint","INTERSECT",VERTEX,{"derivedFrom":[subQ3,subQ0]});Q6=makeQuery(id+"F16.imprint","IMPRINT",FACE,{"disambiguationData":[TD([[makeQuery(id+"F16.imprint","IMPRINT",EDGE,{"disambiguationData":[TD([[subQ4,-1.0]])],"derivedFrom":subQ3}),-1.0]])]});}
            var Q7;
            {var subQ1=sQuery(id+"F16.wireOp",EDGE,"E79.3.0");var subQ6=sQuery(id+"F16.wireOp",EDGE,"E65.0");var subQ8=makeQuery(id+"F16.imprint","INTERSECT",VERTEX,{"derivedFrom":[subQ6,subQ1]});Q7=makeQuery(id+"F16.imprint","IMPRINT",FACE,{"disambiguationData":[TD([[makeQuery(id+"F16.imprint","IMPRINT",EDGE,{"disambiguationData":[TD([[subQ8,-1.0]])],"derivedFrom":subQ6}),1.0]])]});}
            var Q8;
            {var subQ5=sQuery(id+"F16.wireOp",EDGE,"E79.3.5");Q8=makeQuery(id+"F16.imprint","IMPRINT",FACE,{"disambiguationData":[TD([[makeQuery(id+"F16.imprint","IMPRINT",EDGE,{"derivedFrom":subQ5}),1.0]])]});}
            var Q9;
            {var subQ3=sQuery(id+"F16.wireOp",EDGE,"E64");var subQ5=sQuery(id+"F16.wireOp",EDGE,"E79.3.3");var subQ11=makeQuery(id+"F16.imprint","INTERSECT",VERTEX,{"derivedFrom":[subQ3,subQ5]});Q9=makeQuery(id+"F16.imprint","IMPRINT",FACE,{"disambiguationData":[TD([[makeQuery(id+"F16.imprint","IMPRINT",EDGE,{"disambiguationData":[TD([[subQ11,1.0]])],"derivedFrom":subQ3}),-1.0]])]});}
            var Q10;
            {var subQ5=sQuery(id+"F16.wireOp",EDGE,"E79.2.5");Q10=makeQuery(id+"F16.imprint","IMPRINT",FACE,{"disambiguationData":[TD([[makeQuery(id+"F16.imprint","IMPRINT",EDGE,{"derivedFrom":subQ5}),1.0]])]});}
            var Q11;
            {var subQ1=sQuery(id+"F16.wireOp",EDGE,"E79.2.2");var subQ3=sQuery(id+"F16.wireOp",EDGE,"E65.0");var subQ4=makeQuery(id+"F16.imprint","INTERSECT",VERTEX,{"derivedFrom":[subQ3,subQ1]});Q11=makeQuery(id+"F16.imprint","IMPRINT",FACE,{"disambiguationData":[TD([[makeQuery(id+"F16.imprint","IMPRINT",EDGE,{"disambiguationData":[TD([[subQ4,1.0]])],"derivedFrom":subQ3}),1.0]])]});}
            var Q12;
            {var subQ7=sQuery(id+"F16.wireOp",EDGE,"E79.2.3");var subQ9=sQuery(id+"F16.wireOp",EDGE,"E64");var subQ10=makeQuery(id+"F16.imprint","INTERSECT",VERTEX,{"derivedFrom":[subQ9,subQ7]});Q12=makeQuery(id+"F16.imprint","IMPRINT",FACE,{"disambiguationData":[TD([[makeQuery(id+"F16.imprint","IMPRINT",EDGE,{"disambiguationData":[TD([[subQ10,1.0]])],"derivedFrom":subQ9}),-1.0]])]});}
            var Q13;
            {var subQ3=sQuery(id+"F16.wireOp",EDGE,"E65.0");var subQ5=sQuery(id+"F16.wireOp",EDGE,"E79.1.0");var subQ7=makeQuery(id+"F16.imprint","INTERSECT",VERTEX,{"derivedFrom":[subQ3,subQ5]});Q13=makeQuery(id+"F16.imprint","IMPRINT",FACE,{"disambiguationData":[TD([[makeQuery(id+"F16.imprint","IMPRINT",EDGE,{"disambiguationData":[TD([[subQ7,-1.0]])],"derivedFrom":subQ3}),1.0]])]});}
            var Q14;
            {var subQ5=sQuery(id+"F16.wireOp",EDGE,"E79.1.5");Q14=makeQuery(id+"F16.imprint","IMPRINT",FACE,{"disambiguationData":[TD([[makeQuery(id+"F16.imprint","IMPRINT",EDGE,{"derivedFrom":subQ5}),1.0]])]});}
            extrude(context, id + "F17", {"entities" : qUnion([Q0, Q1, Q2, Q3, Q4, Q5, Q6, Q7, Q8, Q9, Q10, Q11, Q12, Q13, Q14]), "operationType" : NewBodyOperationType.ADD, "depth" : 3 * mm});
        }
    });
